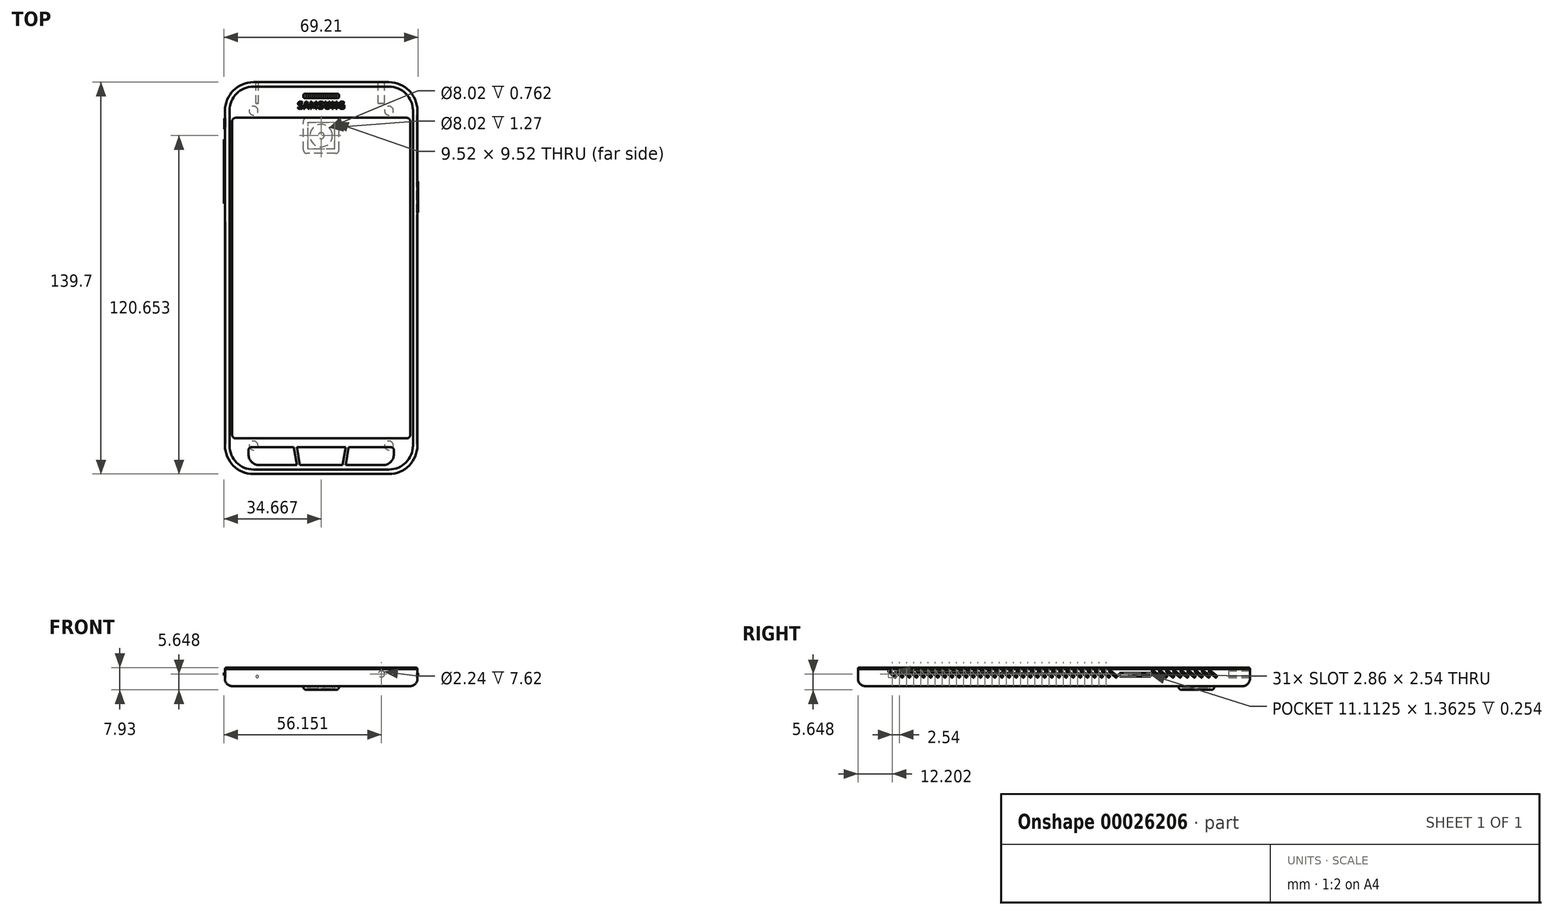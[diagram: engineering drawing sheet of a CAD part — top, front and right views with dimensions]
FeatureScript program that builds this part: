
annotation { "Feature Type Name" : "Feature", "Feature Type Description" : "" }
export const myFeature = defineFeature(function(context is Context, id is Id, definition is map)
    precondition{}
    {
        {
            var Q0;
            Q0=qCreatedBy(makeId("Top.planeOp"),FACE);
            var sketch = newSketch(context, id + "F0", { "sketchPlane" : qUnion([Q0])});
            skLineSegment(sketch, "E0.bottom", {"start": v(-52.33, 67.24) * mm, "end": v(16.25, 67.24) * mm});
            skLineSegment(sketch, "E0.top", {"start": v(-52.33, -72.46) * mm, "end": v(16.25, -72.46) * mm});
            skLineSegment(sketch, "E0.left", {"start": v(-52.33, 67.24) * mm, "end": v(-52.33, -72.46) * mm});
            skLineSegment(sketch, "E0.right", {"start": v(16.25, 67.24) * mm, "end": v(16.25, -72.46) * mm});
            skSolve(sketch);
        }
        {
            var Q0;
            Q0 = qSketchRegion(id + "F0", true);
            extrude(context, id + "F1", {"entities" : qUnion([Q0]), "depth" : 6.1 * mm});
        }
        {
            var Q0;
            Q0=makeQuery(id+"F1.opExtrude","SWEPT_EDGE",EDGE,{"disambiguationData":[OSD([sQuery(id+"F0.wireOp",EDGE,"E0.bottom"),sQuery(id+"F0.wireOp",EDGE,"E0.right")])]});
            var Q1;
            Q1=makeQuery(id+"F1.opExtrude","SWEPT_EDGE",EDGE,{"disambiguationData":[OSD([sQuery(id+"F0.wireOp",EDGE,"E0.top"),sQuery(id+"F0.wireOp",EDGE,"E0.right")])]});
            var Q2;
            Q2=makeQuery(id+"F1.opExtrude","SWEPT_EDGE",EDGE,{"disambiguationData":[OSD([sQuery(id+"F0.wireOp",EDGE,"E0.top"),sQuery(id+"F0.wireOp",EDGE,"E0.left")])]});
            var Q3;
            Q3=makeQuery(id+"F1.opExtrude","SWEPT_EDGE",EDGE,{"disambiguationData":[OSD([sQuery(id+"F0.wireOp",EDGE,"E0.bottom"),sQuery(id+"F0.wireOp",EDGE,"E0.left")])]});
            fillet(context, id + "F2", {"entities" : qUnion([Q0, Q1, Q2, Q3]), "radius" : 10.16 * mm, "tangentPropagation" : true, "allowEdgeOverflow" : false});
        }
        {
            var Q0;
            Q0=makeQuery(id+"F1.opExtrude","CAP_FACE",FACE,{"disambiguationData":[OSD([sQuery(id+"F0.wireOp",EDGE,"E0.bottom"),sQuery(id+"F0.wireOp",EDGE,"E0.top"),sQuery(id+"F0.wireOp",EDGE,"E0.left"),sQuery(id+"F0.wireOp",EDGE,"E0.right")])],"isStart":false});
            var sketch = newSketch(context, id + "F3", { "sketchPlane" : qUnion([Q0])});
            skArc(sketch, "E1.0", {"start": v(13.7, 57.08) * mm, "mid": v(11.48, 62.47) * mm, "end": v(6.09, 64.7) * mm, "construction": true});
            skLineSegment(sketch, "E1.1", {"start": v(13.7, -62.3) * mm, "end": v(13.7, 57.08) * mm, "construction": true});
            skArc(sketch, "E1.2", {"start": v(6.09, -69.92) * mm, "mid": v(11.48, -67.69) * mm, "end": v(13.7, -62.3) * mm, "construction": true});
            skLineSegment(sketch, "E1.3", {"start": v(-42.17, -69.92) * mm, "end": v(6.09, -69.92) * mm, "construction": true});
            skArc(sketch, "E1.4", {"start": v(-49.8, -62.3) * mm, "mid": v(-47.56, -67.69) * mm, "end": v(-42.17, -69.92) * mm, "construction": true});
            skLineSegment(sketch, "E1.5", {"start": v(6.09, 64.7) * mm, "end": v(-42.17, 64.7) * mm, "construction": true});
            skLineSegment(sketch, "E1.6", {"start": v(-49.8, 57.08) * mm, "end": v(-49.8, -62.3) * mm, "construction": true});
            skArc(sketch, "E1.7", {"start": v(-42.17, 64.7) * mm, "mid": v(-47.56, 62.47) * mm, "end": v(-49.8, 57.08) * mm, "construction": true});
            skLineSegment(sketch, "E2.0", {"start": v(-42.17, 54.54) * mm, "end": v(6.09, 54.54) * mm});
            skLineSegment(sketch, "E3.0", {"start": v(-42.17, -59.76) * mm, "end": v(6.09, -59.76) * mm});
            skLineSegment(sketch, "E4", {"start": v(-42.17, 54.54) * mm, "end": v(-48.52, 54.54) * mm});
            skLineSegment(sketch, "E5", {"start": v(6.09, 54.54) * mm, "end": v(12.44, 54.54) * mm});
            skLineSegment(sketch, "E6", {"start": v(6.09, -59.76) * mm, "end": v(12.44, -59.76) * mm});
            skLineSegment(sketch, "E7", {"start": v(13.7, -58.49) * mm, "end": v(13.7, 53.27) * mm});
            skLineSegment(sketch, "E8", {"start": v(-42.17, -59.76) * mm, "end": v(-48.52, -59.76) * mm});
            skLineSegment(sketch, "E9", {"start": v(-49.8, -58.49) * mm, "end": v(-49.8, 53.27) * mm});
            skPoint(sketch, "E10.visualSharp", {"position": v(-49.8, 54.54) * mm});
            skArc(sketch, "E10.filletArc", {"start": v(-48.52, 54.54) * mm, "mid": v(-49.42, 54.17) * mm, "end": v(-49.8, 53.27) * mm});
            skPoint(sketch, "E11.visualSharp", {"position": v(13.7, 54.54) * mm});
            skArc(sketch, "E11.filletArc", {"start": v(13.7, 53.27) * mm, "mid": v(13.34, 54.17) * mm, "end": v(12.44, 54.54) * mm});
            skPoint(sketch, "E12.visualSharp", {"position": v(13.7, -59.76) * mm});
            skArc(sketch, "E12.filletArc", {"start": v(12.44, -59.76) * mm, "mid": v(13.34, -59.39) * mm, "end": v(13.7, -58.49) * mm});
            skPoint(sketch, "E13.visualSharp", {"position": v(-49.8, -59.76) * mm});
            skArc(sketch, "E13.filletArc", {"start": v(-49.8, -58.49) * mm, "mid": v(-49.42, -59.39) * mm, "end": v(-48.52, -59.76) * mm});
            skSolve(sketch);
        }
        {
            var Q0;
            Q0=makeQuery(id+"F3.imprint","IMPRINT",FACE,{"disambiguationData":[TD([[makeQuery(id+"F3.imprint","IMPRINT",EDGE,{"derivedFrom":sQuery(id+"F3.wireOp",EDGE,"E2.0")}),-1.0]])]});
            extrude(context, id + "F4", {"entities" : qUnion([Q0]), "operationType" : NewBodyOperationType.REMOVE, "oppositeDirection" : true, "depth" : 0.03 * mm});
        }
        {
            var Q0;
            Q0 = qSketchRegion(id + "F3", true);
            extrude(context, id + "F5", {"entities" : qUnion([Q0]), "depth" : 0.03 * mm});
        }
        {
            var Q0;
            {var subQ0=sQuery(id+"F0.wireOp",EDGE,"E0.bottom");var subQ1=sQuery(id+"F0.wireOp",EDGE,"E0.right");Q0=makeQuery(id+"F2.opFillet","BLEND_EDGE",EDGE,{"blendedFrom":[makeQuery(id+"F1.opExtrude","SWEPT_EDGE",EDGE,{"disambiguationData":[OSD([subQ0,subQ1])]}),makeQuery(id+"F1.opExtrude","CAP_FACE",FACE,{"disambiguationData":[OSD([subQ0,sQuery(id+"F0.wireOp",EDGE,"E0.top"),sQuery(id+"F0.wireOp",EDGE,"E0.left"),subQ1])],"isStart":true})],"blendedInto":[makeQuery(id+"F1.opExtrude","CAP_FACE",FACE,{"disambiguationData":[OSD([subQ0,sQuery(id+"F0.wireOp",EDGE,"E0.top"),sQuery(id+"F0.wireOp",EDGE,"E0.left"),subQ1])],"isStart":true})]});}
            fillet(context, id + "F6", {"entities" : qUnion([Q0]), "radius" : 2.54 * mm, "tangentPropagation" : true, "allowEdgeOverflow" : false});
        }
        {
            var Q0;
            Q0=makeQuery(id+"F1.opExtrude","CAP_FACE",FACE,{"disambiguationData":[OSD([sQuery(id+"F0.wireOp",EDGE,"E0.bottom"),sQuery(id+"F0.wireOp",EDGE,"E0.top"),sQuery(id+"F0.wireOp",EDGE,"E0.left"),sQuery(id+"F0.wireOp",EDGE,"E0.right")])],"isStart":false});
            var sketch = newSketch(context, id + "F7", { "sketchPlane" : qUnion([Q0])});
            skLineSegment(sketch, "E14", {"start": v(-18.04, 67.24) * mm, "end": v(-18.04, 63.11) * mm, "construction": true});
            skLineSegment(sketch, "E15.0", {"start": v(-48.52, 61.53) * mm, "end": v(12.44, 61.53) * mm, "construction": true});
            skLineSegment(sketch, "E16.bottom", {"start": v(-18.04, 61.53) * mm, "end": v(-11.7, 61.53) * mm});
            skLineSegment(sketch, "E16.top", {"start": v(-18.04, 63.11) * mm, "end": v(-11.7, 63.11) * mm});
            skLineSegment(sketch, "E16.right", {"start": v(-11.7, 61.53) * mm, "end": v(-11.7, 63.11) * mm});
            skLineSegment(sketch, "E17.MirrorCS", {"start": v(-18.04, 63.11) * mm, "end": v(-24.4, 63.11) * mm});
            skLineSegment(sketch, "E18.MirrorCS", {"start": v(-18.04, 61.53) * mm, "end": v(-24.4, 61.53) * mm});
            skLineSegment(sketch, "E19.MirrorCS", {"start": v(-24.4, 61.53) * mm, "end": v(-24.4, 63.11) * mm});
            skLineSegment(sketch, "E20.trimOffspring", {"start": v(-18.04, 61.53) * mm, "end": v(-18.04, -72.46) * mm, "construction": true});
            skArc(sketch, "E21.0", {"start": v(14.66, 57.08) * mm, "mid": v(12.15, 63.14) * mm, "end": v(6.09, 65.65) * mm});
            skLineSegment(sketch, "E21.1", {"start": v(14.66, -62.3) * mm, "end": v(14.66, 57.08) * mm});
            skArc(sketch, "E21.2", {"start": v(6.09, -70.87) * mm, "mid": v(12.15, -68.36) * mm, "end": v(14.66, -62.3) * mm});
            skLineSegment(sketch, "E21.3", {"start": v(-42.17, -70.87) * mm, "end": v(6.09, -70.87) * mm});
            skArc(sketch, "E21.4", {"start": v(-50.75, -62.3) * mm, "mid": v(-48.23, -68.36) * mm, "end": v(-42.17, -70.87) * mm});
            skLineSegment(sketch, "E21.5", {"start": v(6.09, 65.65) * mm, "end": v(-42.17, 65.65) * mm});
            skLineSegment(sketch, "E21.6", {"start": v(-50.75, 57.08) * mm, "end": v(-50.75, -62.3) * mm});
            skArc(sketch, "E21.7", {"start": v(-42.17, 65.65) * mm, "mid": v(-48.23, 63.14) * mm, "end": v(-50.75, 57.08) * mm});
            skArc(sketch, "E22.0", {"start": v(16.25, 57.08) * mm, "mid": v(13.27, 64.27) * mm, "end": v(6.09, 67.24) * mm});
            skLineSegment(sketch, "E22.1", {"start": v(16.25, -62.3) * mm, "end": v(16.25, 57.08) * mm});
            skArc(sketch, "E22.2", {"start": v(6.09, -72.46) * mm, "mid": v(13.27, -69.48) * mm, "end": v(16.25, -62.3) * mm});
            skLineSegment(sketch, "E22.3", {"start": v(-42.17, -72.46) * mm, "end": v(6.09, -72.46) * mm});
            skArc(sketch, "E22.4", {"start": v(-52.33, -62.3) * mm, "mid": v(-49.36, -69.48) * mm, "end": v(-42.17, -72.46) * mm});
            skLineSegment(sketch, "E22.5", {"start": v(6.09, 67.24) * mm, "end": v(-42.17, 67.24) * mm});
            skLineSegment(sketch, "E22.6", {"start": v(-52.33, 57.08) * mm, "end": v(-52.33, -62.3) * mm});
            skArc(sketch, "E22.7", {"start": v(-42.17, 67.24) * mm, "mid": v(-49.36, 64.27) * mm, "end": v(-52.33, 57.08) * mm});
            skLineSegment(sketch, "E23.0", {"start": v(12.44, -69.28) * mm, "end": v(-47.5, -69.28) * mm, "construction": true});
            skLineSegment(sketch, "E24.bottom", {"start": v(-17.53, -69.28) * mm, "end": v(-7.82, -69.28) * mm});
            skLineSegment(sketch, "E24.top", {"start": v(-18.55, -62.93) * mm, "end": v(-9.34, -62.93) * mm});
            skLineSegment(sketch, "E24.right", {"start": v(7.87, -65.47) * mm, "end": v(7.87, -63.95) * mm});
            skLineSegment(sketch, "E25.MirrorCS", {"start": v(-17.53, -62.93) * mm, "end": v(-26.75, -62.93) * mm});
            skLineSegment(sketch, "E26.MirrorCS", {"start": v(-43.95, -65.47) * mm, "end": v(-43.95, -63.95) * mm});
            skLineSegment(sketch, "E27.MirrorCS", {"start": v(-18.55, -69.28) * mm, "end": v(-28.27, -69.28) * mm});
            skPoint(sketch, "E28.visualSharp", {"position": v(-43.95, -62.93) * mm});
            skArc(sketch, "E28.filletArc", {"start": v(-42.93, -62.93) * mm, "mid": v(-43.65, -63.23) * mm, "end": v(-43.95, -63.95) * mm});
            skPoint(sketch, "E29.visualSharp", {"position": v(7.87, -62.93) * mm});
            skArc(sketch, "E29.filletArc", {"start": v(7.87, -63.95) * mm, "mid": v(7.57, -63.23) * mm, "end": v(6.85, -62.93) * mm});
            skPoint(sketch, "E30.visualSharp", {"position": v(-43.95, -69.28) * mm});
            skArc(sketch, "E30.filletArc", {"start": v(-43.95, -65.47) * mm, "mid": v(-42.83, -68.17) * mm, "end": v(-40.14, -69.28) * mm});
            skPoint(sketch, "E31.visualSharp", {"position": v(7.87, -69.28) * mm});
            skArc(sketch, "E31.filletArc", {"start": v(4.06, -69.28) * mm, "mid": v(6.75, -68.17) * mm, "end": v(7.87, -65.47) * mm});
            skLineSegment(sketch, "E32", {"start": v(-18.04, -66.4) * mm, "end": v(-8.52, -66.4) * mm, "construction": true});
            skLineSegment(sketch, "E33.trimOffspring", {"start": v(-27.84, -62.93) * mm, "end": v(-42.93, -62.93) * mm});
            skLineSegment(sketch, "E34.trimOffspring", {"start": v(-29.36, -69.28) * mm, "end": v(-40.14, -69.28) * mm});
            skLineSegment(sketch, "E35.trimOffspring", {"start": v(-8.25, -62.93) * mm, "end": v(6.85, -62.93) * mm});
            skLineSegment(sketch, "E36.trimOffspring", {"start": v(-6.73, -69.28) * mm, "end": v(4.06, -69.28) * mm});
            skLineSegment(sketch, "E37", {"start": v(-18.55, -69.28) * mm, "end": v(-17.53, -69.28) * mm});
            skLineSegment(sketch, "E38", {"start": v(-24.4, 62.32) * mm, "end": v(-11.7, 62.32) * mm, "construction": true});
            skCircle(sketch, "E39", {"center": v(-18.04, 62.32) * mm, "radius": 0.13 * mm});
            skCircle(sketch, "E40.1.0.0", {"center": v(-17.28, 62.32) * mm, "radius": 0.13 * mm});
            skCircle(sketch, "E40.2.0.0", {"center": v(-16.52, 62.32) * mm, "radius": 0.13 * mm});
            skCircle(sketch, "E40.3.0.0", {"center": v(-15.76, 62.32) * mm, "radius": 0.13 * mm});
            skCircle(sketch, "E40.4.0.0", {"center": v(-15, 62.32) * mm, "radius": 0.13 * mm});
            skCircle(sketch, "E40.5.0.0", {"center": v(-14.23, 62.32) * mm, "radius": 0.13 * mm});
            skCircle(sketch, "E40.6.0.0", {"center": v(-13.47, 62.32) * mm, "radius": 0.13 * mm});
            skCircle(sketch, "E40.7.0.0", {"center": v(-12.7, 62.32) * mm, "radius": 0.13 * mm});
            skLineSegment(sketch, "E40.direction1", {"start": v(-18.04, 62.32) * mm, "end": v(-17.28, 62.32) * mm, "construction": true});
            skCircle(sketch, "E41.1.0.0", {"center": v(-18.8, 62.32) * mm, "radius": 0.13 * mm});
            skCircle(sketch, "E41.2.0.0", {"center": v(-19.57, 62.32) * mm, "radius": 0.13 * mm});
            skCircle(sketch, "E41.3.0.0", {"center": v(-20.33, 62.32) * mm, "radius": 0.13 * mm});
            skCircle(sketch, "E41.4.0.0", {"center": v(-21.1, 62.32) * mm, "radius": 0.13 * mm});
            skCircle(sketch, "E41.5.0.0", {"center": v(-21.85, 62.32) * mm, "radius": 0.13 * mm});
            skCircle(sketch, "E41.6.0.0", {"center": v(-22.61, 62.32) * mm, "radius": 0.13 * mm});
            skCircle(sketch, "E41.7.0.0", {"center": v(-23.38, 62.32) * mm, "radius": 0.13 * mm});
            skLineSegment(sketch, "E41.direction1", {"start": v(-18.04, 62.32) * mm, "end": v(-18.8, 62.32) * mm, "construction": true});
            skLineSegment(sketch, "E42", {"start": v(-26.75, -62.93) * mm, "end": v(-27.84, -62.93) * mm});
            skLineSegment(sketch, "E43", {"start": v(-28.27, -69.28) * mm, "end": v(-29.36, -69.28) * mm});
            skLineSegment(sketch, "E44", {"start": v(-9.34, -62.93) * mm, "end": v(-8.25, -62.93) * mm});
            skLineSegment(sketch, "E45", {"start": v(-6.73, -69.28) * mm, "end": v(-7.82, -69.28) * mm});
            skLineSegment(sketch, "E46", {"start": v(-8.25, -62.93) * mm, "end": v(-9.34, -69.28) * mm});
            skLineSegment(sketch, "E47", {"start": v(-10.43, -62.93) * mm, "end": v(-10.43, -69.28) * mm, "construction": true});
            skPoint(sketch, "E48.MirrorCS.end.orphan", {"position": v(-10.86, -69.28) * mm});
            skLineSegment(sketch, "E49", {"start": v(-9.34, -62.93) * mm, "end": v(-10.43, -69.28) * mm});
            skPoint(sketch, "E50.orphan", {"position": v(-7.82, -69.28) * mm});
            skPoint(sketch, "E51.MirrorCS.start.orphan", {"position": v(-9.34, -62.93) * mm});
            skLineSegment(sketch, "E52.MirrorCS", {"start": v(-26.75, -62.93) * mm, "end": v(-25.65, -69.28) * mm});
            skLineSegment(sketch, "E53.MirrorCS", {"start": v(-27.84, -62.93) * mm, "end": v(-26.75, -69.28) * mm});
            skSolve(sketch);
        }
        {
            var Q0;
            Q0=makeQuery(id+"F7.imprint","IMPRINT",FACE,{"disambiguationData":[TD([[makeQuery(id+"F7.imprint","IMPRINT",EDGE,{"derivedFrom":sQuery(id+"F7.wireOp",EDGE,"E16.bottom")}),1.0]])]});
            var Q1;
            Q1=makeQuery(id+"F7.imprint","IMPRINT",FACE,{"disambiguationData":[TD([[makeQuery(id+"F7.imprint","IMPRINT",EDGE,{"derivedFrom":sQuery(id+"F7.wireOp",EDGE,"E21.0")}),-1.0]])]});
            var Q2;
            Q2=makeQuery(id+"F7.imprint","IMPRINT",FACE,{"disambiguationData":[TD([[makeQuery(id+"F7.imprint","IMPRINT",EDGE,{"derivedFrom":sQuery(id+"F7.wireOp",EDGE,"E26.MirrorCS")}),-1.0]])]});
            var Q3;
            Q3=makeQuery(id+"F7.imprint","IMPRINT",FACE,{"disambiguationData":[TD([[makeQuery(id+"F7.imprint","IMPRINT",EDGE,{"derivedFrom":sQuery(id+"F7.wireOp",EDGE,"E24.right")}),1.0]])]});
            var Q4;
            {var subQ6=sQuery(id+"F7.wireOp",EDGE,"E24.top");Q4=makeQuery(id+"F7.imprint","IMPRINT",FACE,{"disambiguationData":[TD([[makeQuery(id+"F7.imprint","IMPRINT",EDGE,{"derivedFrom":subQ6}),-1.0]])]});}
            extrude(context, id + "F8", {"entities" : qUnion([Q0, Q1, Q2, Q3, Q4]), "depth" : 0.5 * mm});
        }
        {
            var Q0;
            Q0=makeQuery(id+"F8.opExtrude","SWEPT_EDGE",EDGE,{"disambiguationData":[OSD([sQuery(id+"F7.wireOp",EDGE,"E16.top"),sQuery(id+"F7.wireOp",EDGE,"E16.right")])]});
            var Q1;
            Q1=makeQuery(id+"F8.opExtrude","SWEPT_EDGE",EDGE,{"disambiguationData":[OSD([sQuery(id+"F7.wireOp",EDGE,"E16.bottom"),sQuery(id+"F7.wireOp",EDGE,"E16.right")])]});
            var Q2;
            Q2=makeQuery(id+"F8.opExtrude","SWEPT_EDGE",EDGE,{"disambiguationData":[OSD([sQuery(id+"F7.wireOp",EDGE,"E19.MirrorCS"),sQuery(id+"F7.wireOp",EDGE,"E18.MirrorCS")])]});
            var Q3;
            Q3=makeQuery(id+"F8.opExtrude","SWEPT_EDGE",EDGE,{"disambiguationData":[OSD([sQuery(id+"F7.wireOp",EDGE,"E17.MirrorCS"),sQuery(id+"F7.wireOp",EDGE,"E19.MirrorCS")])]});
            fillet(context, id + "F9", {"entities" : qUnion([Q0, Q1, Q2, Q3]), "radius" : 0.5 * mm, "tangentPropagation" : true, "allowEdgeOverflow" : false});
        }
        {
            var Q0;
            Q0=makeQuery(id+"F8.opExtrude","CAP_EDGE",EDGE,{"disambiguationData":[OSD([sQuery(id+"F7.wireOp",EDGE,"E21.6")])],"isStart":false});
            var Q1;
            Q1=makeQuery(id+"F8.opExtrude","CAP_EDGE",EDGE,{"disambiguationData":[OSD([sQuery(id+"F7.wireOp",EDGE,"E21.1")])],"isStart":false});
            var Q2;
            Q2=makeQuery(id+"F8.opExtrude","CAP_EDGE",EDGE,{"disambiguationData":[OSD([sQuery(id+"F7.wireOp",EDGE,"E21.5")])],"isStart":false});
            var Q3;
            Q3=makeQuery(id+"F8.opExtrude","CAP_EDGE",EDGE,{"disambiguationData":[OSD([sQuery(id+"F7.wireOp",EDGE,"E21.0")])],"isStart":false});
            var Q4;
            Q4=makeQuery(id+"F8.opExtrude","CAP_EDGE",EDGE,{"disambiguationData":[OSD([sQuery(id+"F7.wireOp",EDGE,"E21.7")])],"isStart":false});
            var Q5;
            Q5=makeQuery(id+"F8.opExtrude","CAP_EDGE",EDGE,{"disambiguationData":[OSD([sQuery(id+"F7.wireOp",EDGE,"E21.2")])],"isStart":false});
            var Q6;
            Q6=makeQuery(id+"F8.opExtrude","CAP_EDGE",EDGE,{"disambiguationData":[OSD([sQuery(id+"F7.wireOp",EDGE,"E21.3")])],"isStart":false});
            var Q7;
            Q7=makeQuery(id+"F8.opExtrude","CAP_EDGE",EDGE,{"disambiguationData":[OSD([sQuery(id+"F7.wireOp",EDGE,"E21.4")])],"isStart":false});
            fillet(context, id + "F10", {"entities" : qUnion([Q0, Q1, Q2, Q3, Q4, Q5, Q6, Q7]), "radius" : 0.5 * mm, "tangentPropagation" : true, "allowEdgeOverflow" : false});
        }
        {
            var Q0;
            Q0=makeQuery(id+"F8.opExtrude","CAP_EDGE",EDGE,{"disambiguationData":[OSD([sQuery(id+"F7.wireOp",EDGE,"E22.1")])],"isStart":false});
            var Q1;
            Q1=makeQuery(id+"F8.opExtrude","CAP_EDGE",EDGE,{"disambiguationData":[OSD([sQuery(id+"F7.wireOp",EDGE,"E22.0")])],"isStart":false});
            var Q2;
            Q2=makeQuery(id+"F8.opExtrude","CAP_EDGE",EDGE,{"disambiguationData":[OSD([sQuery(id+"F7.wireOp",EDGE,"E22.5")])],"isStart":false});
            var Q3;
            Q3=makeQuery(id+"F8.opExtrude","CAP_EDGE",EDGE,{"disambiguationData":[OSD([sQuery(id+"F7.wireOp",EDGE,"E22.7")])],"isStart":false});
            var Q4;
            Q4=makeQuery(id+"F8.opExtrude","CAP_EDGE",EDGE,{"disambiguationData":[OSD([sQuery(id+"F7.wireOp",EDGE,"E22.6")])],"isStart":false});
            var Q5;
            Q5=makeQuery(id+"F8.opExtrude","CAP_EDGE",EDGE,{"disambiguationData":[OSD([sQuery(id+"F7.wireOp",EDGE,"E22.4")])],"isStart":false});
            var Q6;
            Q6=makeQuery(id+"F8.opExtrude","CAP_EDGE",EDGE,{"disambiguationData":[OSD([sQuery(id+"F7.wireOp",EDGE,"E22.3")])],"isStart":false});
            var Q7;
            Q7=makeQuery(id+"F8.opExtrude","CAP_EDGE",EDGE,{"disambiguationData":[OSD([sQuery(id+"F7.wireOp",EDGE,"E22.2")])],"isStart":false});
            fillet(context, id + "F11", {"entities" : qUnion([Q0, Q1, Q2, Q3, Q4, Q5, Q6, Q7]), "radius" : 0.5 * mm, "tangentPropagation" : true, "allowEdgeOverflow" : false});
        }
        {
            var Q0;
            Q0=makeQuery(id+"F1.opExtrude","CAP_FACE",FACE,{"disambiguationData":[OSD([sQuery(id+"F0.wireOp",EDGE,"E0.bottom"),sQuery(id+"F0.wireOp",EDGE,"E0.top"),sQuery(id+"F0.wireOp",EDGE,"E0.left"),sQuery(id+"F0.wireOp",EDGE,"E0.right")])],"isStart":true});
            var sketch = newSketch(context, id + "F12", { "sketchPlane" : qUnion([Q0])});
            skPoint(sketch, "E54.visualSharp", {"position": v(-24.4, 59.76) * mm});
            skPoint(sketch, "E55.visualSharp", {"position": v(-11.7, 59.76) * mm});
            skPoint(sketch, "E56.visualSharp", {"position": v(-11.7, 47.06) * mm});
            skPoint(sketch, "E57.visualSharp", {"position": v(-24.4, 47.06) * mm});
            skLineSegment(sketch, "E58", {"start": v(-49.8, 2.6) * mm, "end": v(13.7, 2.6) * mm, "construction": true});
            skLineSegment(sketch, "E59.MirrorCS", {"start": v(-18.04, -52.95) * mm, "end": v(-22.8, -52.95) * mm});
            skLineSegment(sketch, "E60.MirrorCS", {"start": v(-13.28, -43.43) * mm, "end": v(-13.28, -52.95) * mm});
            skLineSegment(sketch, "E61.MirrorCS", {"start": v(-22.8, -43.43) * mm, "end": v(-22.8, -52.95) * mm});
            skLineSegment(sketch, "E62.MirrorCS", {"start": v(-18.04, -52.95) * mm, "end": v(-13.28, -52.95) * mm});
            skLineSegment(sketch, "E63.MirrorCS", {"start": v(-18.04, -43.43) * mm, "end": v(-13.28, -43.43) * mm});
            skLineSegment(sketch, "E64.MirrorCS", {"start": v(-42.17, -41.84) * mm, "end": v(6.09, -41.84) * mm, "construction": true});
            skArc(sketch, "E65.MirrorCS", {"start": v(-12.96, -41.84) * mm, "mid": v(-12.06, -42.21) * mm, "end": v(-11.7, -43.11) * mm});
            skLineSegment(sketch, "E66.MirrorCS", {"start": v(-24.4, -43.11) * mm, "end": v(-24.4, -53.27) * mm});
            skLineSegment(sketch, "E67.MirrorCS", {"start": v(-11.7, -43.11) * mm, "end": v(-11.7, -53.27) * mm});
            skArc(sketch, "E68.MirrorCS", {"start": v(-11.7, -53.27) * mm, "mid": v(-12.06, -54.17) * mm, "end": v(-12.96, -54.54) * mm});
            skLineSegment(sketch, "E69.MirrorCS", {"start": v(-18.04, -54.54) * mm, "end": v(-12.96, -54.54) * mm});
            skArc(sketch, "E70.MirrorCS", {"start": v(-23.12, -54.54) * mm, "mid": v(-24.02, -54.17) * mm, "end": v(-24.4, -53.27) * mm});
            skLineSegment(sketch, "E71.MirrorCS", {"start": v(-18.04, -54.54) * mm, "end": v(-23.12, -54.54) * mm});
            skPoint(sketch, "E72.orphan", {"position": v(6.09, 47.06) * mm});
            skPoint(sketch, "E73.orphan", {"position": v(-42.17, 47.06) * mm});
            skLineSegment(sketch, "E74.MirrorCS", {"start": v(-18.04, -41.84) * mm, "end": v(-12.96, -41.84) * mm, "construction": true});
            skLineSegment(sketch, "E75.MirrorCS", {"start": v(-18.04, -41.84) * mm, "end": v(-23.12, -41.84) * mm});
            skLineSegment(sketch, "E76", {"start": v(-12.96, -41.84) * mm, "end": v(-18.04, -41.84) * mm});
            skPoint(sketch, "E77.top.start.orphan", {"position": v(-18.04, 59.76) * mm});
            skPoint(sketch, "E78.orphan", {"position": v(-18.04, 69.92) * mm});
            skPoint(sketch, "E54.filletArc.start.orphan", {"position": v(-23.12, 59.76) * mm});
            skPoint(sketch, "E79.MirrorCS.end.orphan", {"position": v(-24.4, 58.49) * mm});
            skPoint(sketch, "E80.MirrorCS.end.orphan", {"position": v(-22.8, 58.17) * mm});
            skPoint(sketch, "E80.MirrorCS.start.orphan", {"position": v(-22.8, 48.65) * mm});
            skPoint(sketch, "E81.5.end.orphan", {"position": v(-13.28, 58.17) * mm});
            skPoint(sketch, "E55.filletArc.end.orphan", {"position": v(-12.96, 59.76) * mm});
            skPoint(sketch, "E55.filletArc.start.orphan", {"position": v(-11.7, 58.49) * mm});
            skPoint(sketch, "E81.1.start.orphan", {"position": v(-18.04, 58.17) * mm});
            skPoint(sketch, "E81.4.end.orphan", {"position": v(-13.28, 48.65) * mm});
            skPoint(sketch, "E81.4.start.orphan", {"position": v(-18.04, 48.65) * mm});
            skPoint(sketch, "E82.MirrorCS.end.orphan", {"position": v(-23.12, -41.84) * mm});
            skPoint(sketch, "E82.MirrorCS.start.orphan", {"position": v(-24.4, -43.11) * mm});
            skPoint(sketch, "E56.filletArc.end.orphan", {"position": v(-11.7, 48.33) * mm});
            skPoint(sketch, "E83.MirrorCS.end.orphan", {"position": v(-22.8, -43.43) * mm});
            skPoint(sketch, "E83.MirrorCS.start.orphan", {"position": v(-18.04, -43.43) * mm});
            skPoint(sketch, "E77.bottom.end.orphan", {"position": v(-12.96, 47.06) * mm});
            skPoint(sketch, "E77.bottom.start.orphan", {"position": v(-18.04, 47.06) * mm});
            skPoint(sketch, "E57.filletArc.end.orphan", {"position": v(-23.12, 47.06) * mm});
            skPoint(sketch, "E57.filletArc.start.orphan", {"position": v(-24.4, 48.33) * mm});
            skLineSegment(sketch, "E84", {"start": v(-18.04, -43.43) * mm, "end": v(-22.8, -43.43) * mm});
            skArc(sketch, "E85", {"start": v(-23.12, -41.84) * mm, "mid": v(-24.02, -42.21) * mm, "end": v(-24.4, -43.11) * mm});
            skLineSegment(sketch, "E86", {"start": v(-42.17, -64.7) * mm, "end": v(-42.17, 69.92) * mm, "construction": true});
            skLineSegment(sketch, "E87", {"start": v(6.09, 69.92) * mm, "end": v(6.09, -64.7) * mm, "construction": true});
            skLineSegment(sketch, "E88", {"start": v(13.7, -57.08) * mm, "end": v(-49.8, -57.08) * mm, "construction": true});
            skLineSegment(sketch, "E89", {"start": v(13.7, 62.3) * mm, "end": v(-49.8, 62.3) * mm, "construction": true});
            skCircle(sketch, "E90", {"center": v(-42.17, 62.3) * mm, "radius": 1.59 * mm});
            skCircle(sketch, "E91", {"center": v(6.09, 62.3) * mm, "radius": 1.59 * mm});
            skCircle(sketch, "E92", {"center": v(-42.17, -57.08) * mm, "radius": 1.59 * mm});
            skCircle(sketch, "E93", {"center": v(6.09, -57.08) * mm, "radius": 1.59 * mm});
            skSolve(sketch);
        }
        {
            var Q0;
            Q0=makeQuery(id+"F12.imprint","IMPRINT",FACE,{"disambiguationData":[TD([[makeQuery(id+"F12.imprint","IMPRINT",EDGE,{"derivedFrom":sQuery(id+"F12.wireOp",EDGE,"E59.MirrorCS")}),1.0]])]});
            extrude(context, id + "F13", {"entities" : qUnion([Q0]), "operationType" : NewBodyOperationType.ADD, "depth" : 1.33 * mm});
        }
        {
            var Q0;
            Q0=makeQuery(id+"F13.boolean.opBoolean","SPLIT",FACE,{"disambiguationData":[TD([makeQuery(id+"F13.opExtrude","SWEPT_FACE",FACE,{"disambiguationData":[OSD([sQuery(id+"F12.wireOp",EDGE,"E60.MirrorCS")])]})])],"derivedFrom":makeQuery(id+"F1.opExtrude","CAP_FACE",FACE,{"disambiguationData":[OSD([sQuery(id+"F0.wireOp",EDGE,"E0.bottom"),sQuery(id+"F0.wireOp",EDGE,"E0.top"),sQuery(id+"F0.wireOp",EDGE,"E0.left"),sQuery(id+"F0.wireOp",EDGE,"E0.right")])],"isStart":true})});
            var sketch = newSketch(context, id + "F14", { "sketchPlane" : qUnion([Q0])});
            skLineSegment(sketch, "E94.bottom", {"start": v(-22.8, -43.43) * mm, "end": v(-13.28, -43.43) * mm});
            skLineSegment(sketch, "E94.top", {"start": v(-22.8, -52.95) * mm, "end": v(-13.28, -52.95) * mm});
            skLineSegment(sketch, "E94.left", {"start": v(-22.8, -43.43) * mm, "end": v(-22.8, -52.95) * mm});
            skLineSegment(sketch, "E94.right", {"start": v(-13.28, -43.43) * mm, "end": v(-13.28, -52.95) * mm});
            skLineSegment(sketch, "E95", {"start": v(-18.04, -52.95) * mm, "end": v(-18.04, -43.43) * mm, "construction": true});
            skLineSegment(sketch, "E96", {"start": v(-13.28, -48.2) * mm, "end": v(-22.8, -48.2) * mm, "construction": true});
            skCircle(sketch, "E97", {"center": v(-18.04, -48.2) * mm, "radius": 4 * mm});
            skCircle(sketch, "E98", {"center": v(-18.04, -48.2) * mm, "radius": 1.08 * mm});
            skSolve(sketch);
        }
        {
            var Q0;
            Q0 = qSketchRegion(id + "F14", true);
            var Q1;
            Q1=makeQuery(id+"F14.imprint","IMPRINT",FACE,{"disambiguationData":[TD([[makeQuery(id+"F14.imprint","IMPRINT",EDGE,{"derivedFrom":sQuery(id+"F14.wireOp",EDGE,"E98")}),1.0]])]});
            extrude(context, id + "F15", {"entities" : qUnion([Q0, Q1]), "depth" : 1.27 * mm});
        }
        {
            var Q0;
            Q0=makeQuery(id+"F13.opExtrude","CAP_EDGE",EDGE,{"disambiguationData":[OSD([sQuery(id+"F12.wireOp",EDGE,"E67.MirrorCS")])],"isStart":false});
            var Q1;
            Q1=makeQuery(id+"F13.opExtrude","CAP_EDGE",EDGE,{"disambiguationData":[OSD([sQuery(id+"F12.wireOp",EDGE,"E68.MirrorCS")])],"isStart":false});
            var Q2;
            Q2=makeQuery(id+"F13.opExtrude","CAP_EDGE",EDGE,{"disambiguationData":[OSD([sQuery(id+"F12.wireOp",EDGE,"E65.MirrorCS")])],"isStart":false});
            var Q3;
            Q3=makeQuery(id+"F13.opExtrude","CAP_EDGE",EDGE,{"disambiguationData":[OSD([sQuery(id+"F12.wireOp",EDGE,"E75.MirrorCS"),sQuery(id+"F12.wireOp",EDGE,"E76")])],"isStart":false});
            var Q4;
            Q4=makeQuery(id+"F13.opExtrude","CAP_EDGE",EDGE,{"disambiguationData":[OSD([sQuery(id+"F12.wireOp",EDGE,"E85")])],"isStart":false});
            var Q5;
            Q5=makeQuery(id+"F13.opExtrude","CAP_EDGE",EDGE,{"disambiguationData":[OSD([sQuery(id+"F12.wireOp",EDGE,"E66.MirrorCS")])],"isStart":false});
            var Q6;
            Q6=makeQuery(id+"F13.opExtrude","CAP_EDGE",EDGE,{"disambiguationData":[OSD([sQuery(id+"F12.wireOp",EDGE,"E70.MirrorCS")])],"isStart":false});
            var Q7;
            Q7=makeQuery(id+"F13.opExtrude","CAP_EDGE",EDGE,{"disambiguationData":[OSD([sQuery(id+"F12.wireOp",EDGE,"E69.MirrorCS"),sQuery(id+"F12.wireOp",EDGE,"E71.MirrorCS")])],"isStart":false});
            fillet(context, id + "F16", {"entities" : qUnion([Q0, Q1, Q2, Q3, Q4, Q5, Q6, Q7]), "radius" : 1.02 * mm, "tangentPropagation" : true, "allowEdgeOverflow" : false});
        }
        {
            var Q0;
            Q0=makeQuery(id+"F1.opExtrude","SWEPT_FACE",FACE,{"disambiguationData":[OSD([sQuery(id+"F0.wireOp",EDGE,"E0.left")])]});
            var sketch = newSketch(context, id + "F17", { "sketchPlane" : qUnion([Q0])});
            skLineSegment(sketch, "E99", {"start": v(61.3, 6.1) * mm, "end": v(61.3, 5.2) * mm, "construction": true});
            skPoint(sketch, "E100.end.orphan", {"position": v(61.3, 5.2) * mm});
            skPoint(sketch, "E101.start.orphan", {"position": v(59.2, 3.43) * mm});
            skPoint(sketch, "E102.start.orphan", {"position": v(59.2, 2.54) * mm});
            skLineSegment(sketch, "E103", {"start": v(59.2, 2.54) * mm, "end": v(59.2, 6.1) * mm, "construction": true});
            skLineSegment(sketch, "E104", {"start": v(61.3, 6.1) * mm, "end": v(61.3, 2.54) * mm, "construction": true});
            skLineSegment(sketch, "E105", {"start": v(61.3, 4.32) * mm, "end": v(59.2, 4.32) * mm, "construction": true});
            skLineSegment(sketch, "E106", {"start": v(59.2, 4.32) * mm, "end": v(59.2, 3.43) * mm, "construction": true});
            skLineSegment(sketch, "E107", {"start": v(61.3, 4.32) * mm, "end": v(61.3, 5.2) * mm, "construction": true});
            skLineSegment(sketch, "E108", {"start": v(58.72, 4.01) * mm, "end": v(60.81, 5.79) * mm, "construction": true});
            skLineSegment(sketch, "E109", {"start": v(61.06, 5.5) * mm, "end": v(60.81, 5.79) * mm, "construction": true});
            skLineSegment(sketch, "E110", {"start": v(58.96, 3.72) * mm, "end": v(58.72, 4.01) * mm, "construction": true});
            skLineSegment(sketch, "E111", {"start": v(59.2, 3.43) * mm, "end": v(61.3, 5.2) * mm, "construction": true});
            skLineSegment(sketch, "E112", {"start": v(59.46, 3.14) * mm, "end": v(61.55, 4.92) * mm});
            skLineSegment(sketch, "E113", {"start": v(61.06, 5.5) * mm, "end": v(58.96, 3.72) * mm});
            skArc(sketch, "E114", {"start": v(58.96, 3.72) * mm, "mid": v(58.92, 3.18) * mm, "end": v(59.46, 3.14) * mm});
            skArc(sketch, "E115", {"start": v(61.55, 4.92) * mm, "mid": v(61.6, 5.45) * mm, "end": v(61.06, 5.5) * mm});
            skLineSegment(sketch, "E116", {"start": v(61.3, 3.55) * mm, "end": v(62.3, 3.55) * mm, "construction": true});
            skLineSegment(sketch, "E117.1.0.0", {"start": v(58.52, 5.5) * mm, "end": v(56.42, 3.72) * mm});
            skArc(sketch, "E117.1.0.1", {"start": v(59.01, 4.92) * mm, "mid": v(59.06, 5.45) * mm, "end": v(58.52, 5.5) * mm});
            skLineSegment(sketch, "E117.1.0.2", {"start": v(56.92, 3.14) * mm, "end": v(59.01, 4.92) * mm});
            skArc(sketch, "E117.1.0.3", {"start": v(56.42, 3.72) * mm, "mid": v(56.38, 3.18) * mm, "end": v(56.92, 3.14) * mm});
            skLineSegment(sketch, "E117.2.0.0", {"start": v(55.98, 5.5) * mm, "end": v(53.88, 3.72) * mm});
            skArc(sketch, "E117.2.0.1", {"start": v(56.47, 4.92) * mm, "mid": v(56.52, 5.45) * mm, "end": v(55.98, 5.5) * mm});
            skLineSegment(sketch, "E117.2.0.2", {"start": v(54.38, 3.14) * mm, "end": v(56.47, 4.92) * mm});
            skArc(sketch, "E117.2.0.3", {"start": v(53.88, 3.72) * mm, "mid": v(53.84, 3.18) * mm, "end": v(54.38, 3.14) * mm});
            skLineSegment(sketch, "E117.3.0.0", {"start": v(53.44, 5.5) * mm, "end": v(51.34, 3.72) * mm});
            skArc(sketch, "E117.3.0.1", {"start": v(53.93, 4.92) * mm, "mid": v(53.98, 5.45) * mm, "end": v(53.44, 5.5) * mm});
            skLineSegment(sketch, "E117.3.0.2", {"start": v(51.84, 3.14) * mm, "end": v(53.93, 4.92) * mm});
            skArc(sketch, "E117.3.0.3", {"start": v(51.34, 3.72) * mm, "mid": v(51.3, 3.18) * mm, "end": v(51.84, 3.14) * mm});
            skLineSegment(sketch, "E117.4.0.0", {"start": v(50.9, 5.5) * mm, "end": v(48.8, 3.72) * mm});
            skArc(sketch, "E117.4.0.1", {"start": v(51.4, 4.92) * mm, "mid": v(51.44, 5.45) * mm, "end": v(50.9, 5.5) * mm});
            skLineSegment(sketch, "E117.4.0.2", {"start": v(49.3, 3.14) * mm, "end": v(51.4, 4.92) * mm});
            skArc(sketch, "E117.4.0.3", {"start": v(48.8, 3.72) * mm, "mid": v(48.76, 3.18) * mm, "end": v(49.3, 3.14) * mm});
            skLineSegment(sketch, "E117.5.0.0", {"start": v(48.36, 5.5) * mm, "end": v(46.26, 3.72) * mm});
            skArc(sketch, "E117.5.0.1", {"start": v(48.85, 4.92) * mm, "mid": v(48.9, 5.45) * mm, "end": v(48.36, 5.5) * mm});
            skLineSegment(sketch, "E117.5.0.2", {"start": v(46.76, 3.14) * mm, "end": v(48.85, 4.92) * mm});
            skArc(sketch, "E117.5.0.3", {"start": v(46.26, 3.72) * mm, "mid": v(46.22, 3.18) * mm, "end": v(46.76, 3.14) * mm});
            skLineSegment(sketch, "E117.6.0.0", {"start": v(45.82, 5.5) * mm, "end": v(43.72, 3.72) * mm});
            skArc(sketch, "E117.6.0.1", {"start": v(46.31, 4.92) * mm, "mid": v(46.36, 5.45) * mm, "end": v(45.82, 5.5) * mm});
            skLineSegment(sketch, "E117.6.0.2", {"start": v(44.22, 3.14) * mm, "end": v(46.31, 4.92) * mm});
            skArc(sketch, "E117.6.0.3", {"start": v(43.72, 3.72) * mm, "mid": v(43.68, 3.18) * mm, "end": v(44.22, 3.14) * mm});
            skLineSegment(sketch, "E117.7.0.0", {"start": v(43.28, 5.5) * mm, "end": v(41.18, 3.72) * mm});
            skArc(sketch, "E117.7.0.1", {"start": v(43.77, 4.92) * mm, "mid": v(43.82, 5.45) * mm, "end": v(43.28, 5.5) * mm});
            skLineSegment(sketch, "E117.7.0.2", {"start": v(41.68, 3.14) * mm, "end": v(43.77, 4.92) * mm});
            skArc(sketch, "E117.7.0.3", {"start": v(41.18, 3.72) * mm, "mid": v(41.14, 3.18) * mm, "end": v(41.68, 3.14) * mm});
            skLineSegment(sketch, "E117.8.0.0", {"start": v(40.74, 5.5) * mm, "end": v(38.64, 3.72) * mm});
            skArc(sketch, "E117.8.0.1", {"start": v(41.23, 4.92) * mm, "mid": v(41.28, 5.45) * mm, "end": v(40.74, 5.5) * mm});
            skLineSegment(sketch, "E117.8.0.2", {"start": v(39.14, 3.14) * mm, "end": v(41.23, 4.92) * mm});
            skArc(sketch, "E117.8.0.3", {"start": v(38.64, 3.72) * mm, "mid": v(38.6, 3.18) * mm, "end": v(39.14, 3.14) * mm});
            skLineSegment(sketch, "E117.9.0.0", {"start": v(38.2, 5.5) * mm, "end": v(36.1, 3.72) * mm});
            skArc(sketch, "E117.9.0.1", {"start": v(38.7, 4.92) * mm, "mid": v(38.74, 5.45) * mm, "end": v(38.2, 5.5) * mm});
            skLineSegment(sketch, "E117.9.0.2", {"start": v(36.6, 3.14) * mm, "end": v(38.7, 4.92) * mm});
            skArc(sketch, "E117.9.0.3", {"start": v(36.1, 3.72) * mm, "mid": v(36.06, 3.18) * mm, "end": v(36.6, 3.14) * mm});
            skLineSegment(sketch, "E117.10.0.0", {"start": v(35.66, 5.5) * mm, "end": v(33.56, 3.72) * mm});
            skArc(sketch, "E117.10.0.1", {"start": v(36.15, 4.92) * mm, "mid": v(36.2, 5.45) * mm, "end": v(35.66, 5.5) * mm});
            skLineSegment(sketch, "E117.10.0.2", {"start": v(34.06, 3.14) * mm, "end": v(36.15, 4.92) * mm});
            skArc(sketch, "E117.10.0.3", {"start": v(33.56, 3.72) * mm, "mid": v(33.52, 3.18) * mm, "end": v(34.06, 3.14) * mm});
            skLineSegment(sketch, "E117.11.0.0", {"start": v(33.12, 5.5) * mm, "end": v(31.02, 3.72) * mm});
            skArc(sketch, "E117.11.0.1", {"start": v(33.61, 4.92) * mm, "mid": v(33.66, 5.45) * mm, "end": v(33.12, 5.5) * mm});
            skLineSegment(sketch, "E117.11.0.2", {"start": v(31.52, 3.14) * mm, "end": v(33.61, 4.92) * mm});
            skArc(sketch, "E117.11.0.3", {"start": v(31.02, 3.72) * mm, "mid": v(30.98, 3.18) * mm, "end": v(31.52, 3.14) * mm});
            skLineSegment(sketch, "E117.12.0.0", {"start": v(30.58, 5.5) * mm, "end": v(28.48, 3.72) * mm});
            skArc(sketch, "E117.12.0.1", {"start": v(31.07, 4.92) * mm, "mid": v(31.12, 5.45) * mm, "end": v(30.58, 5.5) * mm});
            skLineSegment(sketch, "E117.12.0.2", {"start": v(28.98, 3.14) * mm, "end": v(31.07, 4.92) * mm});
            skArc(sketch, "E117.12.0.3", {"start": v(28.48, 3.72) * mm, "mid": v(28.44, 3.18) * mm, "end": v(28.98, 3.14) * mm});
            skLineSegment(sketch, "E117.13.0.0", {"start": v(28.04, 5.5) * mm, "end": v(25.94, 3.72) * mm});
            skArc(sketch, "E117.13.0.1", {"start": v(28.53, 4.92) * mm, "mid": v(28.58, 5.45) * mm, "end": v(28.04, 5.5) * mm});
            skLineSegment(sketch, "E117.13.0.2", {"start": v(26.44, 3.14) * mm, "end": v(28.53, 4.92) * mm});
            skArc(sketch, "E117.13.0.3", {"start": v(25.94, 3.72) * mm, "mid": v(25.9, 3.18) * mm, "end": v(26.44, 3.14) * mm});
            skLineSegment(sketch, "E117.14.0.0", {"start": v(25.5, 5.5) * mm, "end": v(23.4, 3.72) * mm});
            skArc(sketch, "E117.14.0.1", {"start": v(26, 4.92) * mm, "mid": v(26.04, 5.45) * mm, "end": v(25.5, 5.5) * mm});
            skLineSegment(sketch, "E117.14.0.2", {"start": v(23.9, 3.14) * mm, "end": v(26, 4.92) * mm});
            skArc(sketch, "E117.14.0.3", {"start": v(23.4, 3.72) * mm, "mid": v(23.36, 3.18) * mm, "end": v(23.9, 3.14) * mm});
            skLineSegment(sketch, "E117.15.0.0", {"start": v(22.96, 5.5) * mm, "end": v(20.86, 3.72) * mm});
            skArc(sketch, "E117.15.0.1", {"start": v(23.45, 4.92) * mm, "mid": v(23.5, 5.45) * mm, "end": v(22.96, 5.5) * mm});
            skLineSegment(sketch, "E117.15.0.2", {"start": v(21.36, 3.14) * mm, "end": v(23.45, 4.92) * mm});
            skArc(sketch, "E117.15.0.3", {"start": v(20.86, 3.72) * mm, "mid": v(20.82, 3.18) * mm, "end": v(21.36, 3.14) * mm});
            skLineSegment(sketch, "E117.16.0.0", {"start": v(20.42, 5.5) * mm, "end": v(18.32, 3.72) * mm});
            skArc(sketch, "E117.16.0.1", {"start": v(20.91, 4.92) * mm, "mid": v(20.96, 5.45) * mm, "end": v(20.42, 5.5) * mm});
            skLineSegment(sketch, "E117.16.0.2", {"start": v(18.82, 3.14) * mm, "end": v(20.91, 4.92) * mm});
            skArc(sketch, "E117.16.0.3", {"start": v(18.32, 3.72) * mm, "mid": v(18.28, 3.18) * mm, "end": v(18.82, 3.14) * mm});
            skLineSegment(sketch, "E117.17.0.0", {"start": v(17.88, 5.5) * mm, "end": v(15.78, 3.72) * mm});
            skArc(sketch, "E117.17.0.1", {"start": v(18.37, 4.92) * mm, "mid": v(18.42, 5.45) * mm, "end": v(17.88, 5.5) * mm});
            skLineSegment(sketch, "E117.17.0.2", {"start": v(16.28, 3.14) * mm, "end": v(18.37, 4.92) * mm});
            skArc(sketch, "E117.17.0.3", {"start": v(15.78, 3.72) * mm, "mid": v(15.74, 3.18) * mm, "end": v(16.28, 3.14) * mm});
            skLineSegment(sketch, "E117.18.0.0", {"start": v(15.34, 5.5) * mm, "end": v(13.24, 3.72) * mm});
            skArc(sketch, "E117.18.0.1", {"start": v(15.83, 4.92) * mm, "mid": v(15.88, 5.45) * mm, "end": v(15.34, 5.5) * mm});
            skLineSegment(sketch, "E117.18.0.2", {"start": v(13.74, 3.14) * mm, "end": v(15.83, 4.92) * mm});
            skArc(sketch, "E117.18.0.3", {"start": v(13.24, 3.72) * mm, "mid": v(13.2, 3.18) * mm, "end": v(13.74, 3.14) * mm});
            skLineSegment(sketch, "E117.19.0.0", {"start": v(12.8, 5.5) * mm, "end": v(10.7, 3.72) * mm});
            skArc(sketch, "E117.19.0.1", {"start": v(13.3, 4.92) * mm, "mid": v(13.34, 5.45) * mm, "end": v(12.8, 5.5) * mm});
            skLineSegment(sketch, "E117.19.0.2", {"start": v(11.2, 3.14) * mm, "end": v(13.3, 4.92) * mm});
            skArc(sketch, "E117.19.0.3", {"start": v(10.7, 3.72) * mm, "mid": v(10.66, 3.18) * mm, "end": v(11.2, 3.14) * mm});
            skLineSegment(sketch, "E117.20.0.0", {"start": v(10.26, 5.5) * mm, "end": v(8.16, 3.72) * mm});
            skArc(sketch, "E117.20.0.1", {"start": v(10.75, 4.92) * mm, "mid": v(10.8, 5.45) * mm, "end": v(10.26, 5.5) * mm});
            skLineSegment(sketch, "E117.20.0.2", {"start": v(8.66, 3.14) * mm, "end": v(10.75, 4.92) * mm});
            skArc(sketch, "E117.20.0.3", {"start": v(8.16, 3.72) * mm, "mid": v(8.12, 3.18) * mm, "end": v(8.66, 3.14) * mm});
            skLineSegment(sketch, "E117.21.0.0", {"start": v(7.72, 5.5) * mm, "end": v(5.62, 3.72) * mm});
            skArc(sketch, "E117.21.0.1", {"start": v(8.21, 4.92) * mm, "mid": v(8.26, 5.45) * mm, "end": v(7.72, 5.5) * mm});
            skLineSegment(sketch, "E117.21.0.2", {"start": v(6.12, 3.14) * mm, "end": v(8.21, 4.92) * mm});
            skArc(sketch, "E117.21.0.3", {"start": v(5.62, 3.72) * mm, "mid": v(5.58, 3.18) * mm, "end": v(6.12, 3.14) * mm});
            skLineSegment(sketch, "E117.22.0.0", {"start": v(5.18, 5.5) * mm, "end": v(3.08, 3.72) * mm});
            skArc(sketch, "E117.22.0.1", {"start": v(5.67, 4.92) * mm, "mid": v(5.72, 5.45) * mm, "end": v(5.18, 5.5) * mm});
            skLineSegment(sketch, "E117.22.0.2", {"start": v(3.58, 3.14) * mm, "end": v(5.67, 4.92) * mm});
            skArc(sketch, "E117.22.0.3", {"start": v(3.08, 3.72) * mm, "mid": v(3.04, 3.18) * mm, "end": v(3.58, 3.14) * mm});
            skLineSegment(sketch, "E117.23.0.0", {"start": v(2.64, 5.5) * mm, "end": v(0.54, 3.72) * mm});
            skArc(sketch, "E117.23.0.1", {"start": v(3.13, 4.92) * mm, "mid": v(3.18, 5.45) * mm, "end": v(2.64, 5.5) * mm});
            skLineSegment(sketch, "E117.23.0.2", {"start": v(1.04, 3.14) * mm, "end": v(3.13, 4.92) * mm});
            skArc(sketch, "E117.23.0.3", {"start": v(0.54, 3.72) * mm, "mid": v(0.5, 3.18) * mm, "end": v(1.04, 3.14) * mm});
            skLineSegment(sketch, "E117.24.0.0", {"start": v(0.1, 5.5) * mm, "end": v(-2, 3.72) * mm});
            skArc(sketch, "E117.24.0.1", {"start": v(0.6, 4.92) * mm, "mid": v(0.64, 5.45) * mm, "end": v(0.1, 5.5) * mm});
            skLineSegment(sketch, "E117.24.0.2", {"start": v(-1.5, 3.14) * mm, "end": v(0.6, 4.92) * mm});
            skArc(sketch, "E117.24.0.3", {"start": v(-2, 3.72) * mm, "mid": v(-2.04, 3.18) * mm, "end": v(-1.5, 3.14) * mm});
            skLineSegment(sketch, "E117.25.0.0", {"start": v(-2.44, 5.5) * mm, "end": v(-4.54, 3.72) * mm});
            skArc(sketch, "E117.25.0.1", {"start": v(-1.95, 4.92) * mm, "mid": v(-1.9, 5.45) * mm, "end": v(-2.44, 5.5) * mm});
            skLineSegment(sketch, "E117.25.0.2", {"start": v(-4.04, 3.14) * mm, "end": v(-1.95, 4.92) * mm});
            skArc(sketch, "E117.25.0.3", {"start": v(-4.54, 3.72) * mm, "mid": v(-4.58, 3.18) * mm, "end": v(-4.04, 3.14) * mm});
            skLineSegment(sketch, "E117.26.0.0", {"start": v(-4.98, 5.5) * mm, "end": v(-7.08, 3.72) * mm});
            skArc(sketch, "E117.26.0.1", {"start": v(-4.49, 4.92) * mm, "mid": v(-4.44, 5.45) * mm, "end": v(-4.98, 5.5) * mm});
            skLineSegment(sketch, "E117.26.0.2", {"start": v(-6.58, 3.14) * mm, "end": v(-4.49, 4.92) * mm});
            skArc(sketch, "E117.26.0.3", {"start": v(-7.08, 3.72) * mm, "mid": v(-7.12, 3.18) * mm, "end": v(-6.58, 3.14) * mm});
            skLineSegment(sketch, "E117.27.0.0", {"start": v(-7.52, 5.5) * mm, "end": v(-9.62, 3.72) * mm});
            skArc(sketch, "E117.27.0.1", {"start": v(-7.03, 4.92) * mm, "mid": v(-6.98, 5.45) * mm, "end": v(-7.52, 5.5) * mm});
            skLineSegment(sketch, "E117.27.0.2", {"start": v(-9.12, 3.14) * mm, "end": v(-7.03, 4.92) * mm});
            skArc(sketch, "E117.27.0.3", {"start": v(-9.62, 3.72) * mm, "mid": v(-9.66, 3.18) * mm, "end": v(-9.12, 3.14) * mm});
            skLineSegment(sketch, "E117.28.0.0", {"start": v(-10.06, 5.5) * mm, "end": v(-12.16, 3.72) * mm});
            skArc(sketch, "E117.28.0.1", {"start": v(-9.57, 4.92) * mm, "mid": v(-9.52, 5.45) * mm, "end": v(-10.06, 5.5) * mm});
            skLineSegment(sketch, "E117.28.0.2", {"start": v(-11.66, 3.14) * mm, "end": v(-9.57, 4.92) * mm});
            skArc(sketch, "E117.28.0.3", {"start": v(-12.16, 3.72) * mm, "mid": v(-12.2, 3.18) * mm, "end": v(-11.66, 3.14) * mm});
            skLineSegment(sketch, "E117.29.0.0", {"start": v(-12.6, 5.5) * mm, "end": v(-14.7, 3.72) * mm});
            skArc(sketch, "E117.29.0.1", {"start": v(-12.1, 4.92) * mm, "mid": v(-12.06, 5.45) * mm, "end": v(-12.6, 5.5) * mm});
            skLineSegment(sketch, "E117.29.0.2", {"start": v(-14.2, 3.14) * mm, "end": v(-12.1, 4.92) * mm});
            skArc(sketch, "E117.29.0.3", {"start": v(-14.7, 3.72) * mm, "mid": v(-14.74, 3.18) * mm, "end": v(-14.2, 3.14) * mm});
            skLineSegment(sketch, "E117.30.0.0", {"start": v(-15.14, 5.5) * mm, "end": v(-17.24, 3.72) * mm});
            skArc(sketch, "E117.30.0.1", {"start": v(-14.65, 4.92) * mm, "mid": v(-14.6, 5.45) * mm, "end": v(-15.14, 5.5) * mm});
            skLineSegment(sketch, "E117.30.0.2", {"start": v(-16.74, 3.14) * mm, "end": v(-14.65, 4.92) * mm});
            skArc(sketch, "E117.30.0.3", {"start": v(-17.24, 3.72) * mm, "mid": v(-17.28, 3.18) * mm, "end": v(-16.74, 3.14) * mm});
            skLineSegment(sketch, "E117.direction1", {"start": v(58.96, 3.72) * mm, "end": v(56.42, 3.72) * mm, "construction": true});
            skLineSegment(sketch, "E118", {"start": v(-57.08, 6.1) * mm, "end": v(-18.98, 6.1) * mm, "construction": true});
            skLineSegment(sketch, "E119", {"start": v(-57.08, 4.32) * mm, "end": v(-18.98, 4.32) * mm, "construction": true});
            skLineSegment(sketch, "E120.rect.bottom", {"start": v(-54.28, 4.83) * mm, "end": v(-50.47, 4.83) * mm});
            skLineSegment(sketch, "E120.rect.top", {"start": v(-54.28, 3.8) * mm, "end": v(-50.47, 3.8) * mm});
            skLineSegment(sketch, "E120.rect.left", {"start": v(-54.28, 4.83) * mm, "end": v(-54.28, 3.81) * mm});
            skLineSegment(sketch, "E120.rect.right", {"start": v(-50.47, 4.83) * mm, "end": v(-50.47, 3.81) * mm});
            skPoint(sketch, "E120.rect.middle", {"position": v(-52.37, 4.32) * mm});
            skLineSegment(sketch, "E121.rect.bottom", {"start": v(-23.95, 4.83) * mm, "end": v(-46.81, 4.83) * mm});
            skLineSegment(sketch, "E121.rect.top", {"start": v(-23.95, 3.81) * mm, "end": v(-46.81, 3.81) * mm});
            skLineSegment(sketch, "E121.rect.left", {"start": v(-23.95, 4.83) * mm, "end": v(-23.95, 3.81) * mm});
            skLineSegment(sketch, "E121.rect.right", {"start": v(-46.81, 4.83) * mm, "end": v(-46.81, 3.81) * mm});
            skPoint(sketch, "E121.rect.middle", {"position": v(-35.38, 4.32) * mm});
            skSolve(sketch);
        }
        {
            var Q0;
            Q0=makeQuery(id+"F1.opExtrude","SWEPT_FACE",FACE,{"disambiguationData":[OSD([sQuery(id+"F0.wireOp",EDGE,"E0.right")])]});
            var sketch = newSketch(context, id + "F18", { "sketchPlane" : qUnion([Q0])});
            skLineSegment(sketch, "E122", {"start": v(-62.3, 3.54) * mm, "end": v(-61.3, 3.54) * mm, "construction": true});
            skLineSegment(sketch, "E123", {"start": v(-61.3, 2.54) * mm, "end": v(-61.3, 6.1) * mm, "construction": true});
            skLineSegment(sketch, "E124", {"start": v(-61.3, 4.32) * mm, "end": v(-59.2, 4.32) * mm, "construction": true});
            skLineSegment(sketch, "E125", {"start": v(-59.2, 2.54) * mm, "end": v(-59.2, 6.1) * mm, "construction": true});
            skLineSegment(sketch, "E126", {"start": v(-61.3, 4.32) * mm, "end": v(-61.3, 5.2) * mm, "construction": true});
            skLineSegment(sketch, "E127", {"start": v(-59.2, 4.32) * mm, "end": v(-59.2, 3.43) * mm, "construction": true});
            skLineSegment(sketch, "E128", {"start": v(-61.3, 5.2) * mm, "end": v(-59.2, 3.43) * mm, "construction": true});
            skLineSegment(sketch, "E129", {"start": v(-59.2, 3.43) * mm, "end": v(-58.72, 4.01) * mm, "construction": true});
            skLineSegment(sketch, "E130", {"start": v(-61.3, 5.2) * mm, "end": v(-60.81, 5.79) * mm, "construction": true});
            skLineSegment(sketch, "E131", {"start": v(-60.81, 5.79) * mm, "end": v(-58.72, 4.01) * mm, "construction": true});
            skLineSegment(sketch, "E132", {"start": v(-61.06, 5.5) * mm, "end": v(-58.96, 3.72) * mm});
            skLineSegment(sketch, "E133", {"start": v(-61.55, 4.92) * mm, "end": v(-59.46, 3.14) * mm});
            skArc(sketch, "E134", {"start": v(-61.06, 5.5) * mm, "mid": v(-61.6, 5.45) * mm, "end": v(-61.55, 4.92) * mm});
            skArc(sketch, "E135", {"start": v(-59.46, 3.14) * mm, "mid": v(-58.92, 3.18) * mm, "end": v(-58.96, 3.72) * mm});
            skLineSegment(sketch, "E136.1.0.0", {"start": v(-58.52, 5.5) * mm, "end": v(-56.42, 3.72) * mm});
            skArc(sketch, "E136.1.0.1", {"start": v(-58.52, 5.5) * mm, "mid": v(-59.06, 5.45) * mm, "end": v(-59.01, 4.92) * mm});
            skLineSegment(sketch, "E136.1.0.2", {"start": v(-59.01, 4.92) * mm, "end": v(-56.92, 3.14) * mm});
            skArc(sketch, "E136.1.0.3", {"start": v(-56.92, 3.14) * mm, "mid": v(-56.38, 3.18) * mm, "end": v(-56.42, 3.72) * mm});
            skLineSegment(sketch, "E136.2.0.0", {"start": v(-55.98, 5.5) * mm, "end": v(-53.88, 3.72) * mm});
            skArc(sketch, "E136.2.0.1", {"start": v(-55.98, 5.5) * mm, "mid": v(-56.52, 5.45) * mm, "end": v(-56.47, 4.92) * mm});
            skLineSegment(sketch, "E136.2.0.2", {"start": v(-56.47, 4.92) * mm, "end": v(-54.38, 3.14) * mm});
            skArc(sketch, "E136.2.0.3", {"start": v(-54.38, 3.14) * mm, "mid": v(-53.84, 3.18) * mm, "end": v(-53.88, 3.72) * mm});
            skLineSegment(sketch, "E136.3.0.0", {"start": v(-53.44, 5.5) * mm, "end": v(-51.34, 3.72) * mm});
            skArc(sketch, "E136.3.0.1", {"start": v(-53.44, 5.5) * mm, "mid": v(-53.98, 5.45) * mm, "end": v(-53.93, 4.92) * mm});
            skLineSegment(sketch, "E136.3.0.2", {"start": v(-53.93, 4.92) * mm, "end": v(-51.84, 3.14) * mm});
            skArc(sketch, "E136.3.0.3", {"start": v(-51.84, 3.14) * mm, "mid": v(-51.3, 3.18) * mm, "end": v(-51.34, 3.72) * mm});
            skLineSegment(sketch, "E136.4.0.0", {"start": v(-50.9, 5.5) * mm, "end": v(-48.8, 3.72) * mm});
            skArc(sketch, "E136.4.0.1", {"start": v(-50.9, 5.5) * mm, "mid": v(-51.44, 5.45) * mm, "end": v(-51.4, 4.92) * mm});
            skLineSegment(sketch, "E136.4.0.2", {"start": v(-51.4, 4.92) * mm, "end": v(-49.3, 3.14) * mm});
            skArc(sketch, "E136.4.0.3", {"start": v(-49.3, 3.14) * mm, "mid": v(-48.76, 3.18) * mm, "end": v(-48.8, 3.72) * mm});
            skLineSegment(sketch, "E136.5.0.0", {"start": v(-48.36, 5.5) * mm, "end": v(-46.26, 3.72) * mm});
            skArc(sketch, "E136.5.0.1", {"start": v(-48.36, 5.5) * mm, "mid": v(-48.9, 5.45) * mm, "end": v(-48.85, 4.92) * mm});
            skLineSegment(sketch, "E136.5.0.2", {"start": v(-48.85, 4.92) * mm, "end": v(-46.76, 3.14) * mm});
            skArc(sketch, "E136.5.0.3", {"start": v(-46.76, 3.14) * mm, "mid": v(-46.22, 3.18) * mm, "end": v(-46.26, 3.72) * mm});
            skLineSegment(sketch, "E136.6.0.0", {"start": v(-45.82, 5.5) * mm, "end": v(-43.72, 3.72) * mm});
            skArc(sketch, "E136.6.0.1", {"start": v(-45.82, 5.5) * mm, "mid": v(-46.36, 5.45) * mm, "end": v(-46.31, 4.92) * mm});
            skLineSegment(sketch, "E136.6.0.2", {"start": v(-46.31, 4.92) * mm, "end": v(-44.22, 3.14) * mm});
            skArc(sketch, "E136.6.0.3", {"start": v(-44.22, 3.14) * mm, "mid": v(-43.68, 3.18) * mm, "end": v(-43.72, 3.72) * mm});
            skLineSegment(sketch, "E136.7.0.0", {"start": v(-43.28, 5.5) * mm, "end": v(-41.18, 3.72) * mm});
            skArc(sketch, "E136.7.0.1", {"start": v(-43.28, 5.5) * mm, "mid": v(-43.82, 5.45) * mm, "end": v(-43.77, 4.92) * mm});
            skLineSegment(sketch, "E136.7.0.2", {"start": v(-43.77, 4.92) * mm, "end": v(-41.68, 3.14) * mm});
            skArc(sketch, "E136.7.0.3", {"start": v(-41.68, 3.14) * mm, "mid": v(-41.14, 3.18) * mm, "end": v(-41.18, 3.72) * mm});
            skLineSegment(sketch, "E136.8.0.0", {"start": v(-40.74, 5.5) * mm, "end": v(-38.64, 3.72) * mm});
            skArc(sketch, "E136.8.0.1", {"start": v(-40.74, 5.5) * mm, "mid": v(-41.28, 5.45) * mm, "end": v(-41.23, 4.92) * mm});
            skLineSegment(sketch, "E136.8.0.2", {"start": v(-41.23, 4.92) * mm, "end": v(-39.14, 3.14) * mm});
            skArc(sketch, "E136.8.0.3", {"start": v(-39.14, 3.14) * mm, "mid": v(-38.6, 3.18) * mm, "end": v(-38.64, 3.72) * mm});
            skLineSegment(sketch, "E136.9.0.0", {"start": v(-38.2, 5.5) * mm, "end": v(-36.1, 3.72) * mm});
            skArc(sketch, "E136.9.0.1", {"start": v(-38.2, 5.5) * mm, "mid": v(-38.74, 5.45) * mm, "end": v(-38.7, 4.92) * mm});
            skLineSegment(sketch, "E136.9.0.2", {"start": v(-38.7, 4.92) * mm, "end": v(-36.6, 3.14) * mm});
            skArc(sketch, "E136.9.0.3", {"start": v(-36.6, 3.14) * mm, "mid": v(-36.06, 3.18) * mm, "end": v(-36.1, 3.72) * mm});
            skLineSegment(sketch, "E136.10.0.0", {"start": v(-35.66, 5.5) * mm, "end": v(-33.56, 3.72) * mm});
            skArc(sketch, "E136.10.0.1", {"start": v(-35.66, 5.5) * mm, "mid": v(-36.2, 5.45) * mm, "end": v(-36.15, 4.92) * mm});
            skLineSegment(sketch, "E136.10.0.2", {"start": v(-36.15, 4.92) * mm, "end": v(-34.06, 3.14) * mm});
            skArc(sketch, "E136.10.0.3", {"start": v(-34.06, 3.14) * mm, "mid": v(-33.52, 3.18) * mm, "end": v(-33.56, 3.72) * mm});
            skLineSegment(sketch, "E136.11.0.0", {"start": v(-33.12, 5.5) * mm, "end": v(-31.02, 3.72) * mm});
            skArc(sketch, "E136.11.0.1", {"start": v(-33.12, 5.5) * mm, "mid": v(-33.66, 5.45) * mm, "end": v(-33.61, 4.92) * mm});
            skLineSegment(sketch, "E136.11.0.2", {"start": v(-33.61, 4.92) * mm, "end": v(-31.52, 3.14) * mm});
            skArc(sketch, "E136.11.0.3", {"start": v(-31.52, 3.14) * mm, "mid": v(-30.98, 3.18) * mm, "end": v(-31.02, 3.72) * mm});
            skLineSegment(sketch, "E136.12.0.0", {"start": v(-30.58, 5.5) * mm, "end": v(-28.48, 3.72) * mm});
            skArc(sketch, "E136.12.0.1", {"start": v(-30.58, 5.5) * mm, "mid": v(-31.12, 5.45) * mm, "end": v(-31.07, 4.92) * mm});
            skLineSegment(sketch, "E136.12.0.2", {"start": v(-31.07, 4.92) * mm, "end": v(-28.98, 3.14) * mm});
            skArc(sketch, "E136.12.0.3", {"start": v(-28.98, 3.14) * mm, "mid": v(-28.44, 3.18) * mm, "end": v(-28.48, 3.72) * mm});
            skLineSegment(sketch, "E136.13.0.0", {"start": v(-28.04, 5.5) * mm, "end": v(-25.94, 3.72) * mm});
            skArc(sketch, "E136.13.0.1", {"start": v(-28.04, 5.5) * mm, "mid": v(-28.58, 5.45) * mm, "end": v(-28.53, 4.92) * mm});
            skLineSegment(sketch, "E136.13.0.2", {"start": v(-28.53, 4.92) * mm, "end": v(-26.44, 3.14) * mm});
            skArc(sketch, "E136.13.0.3", {"start": v(-26.44, 3.14) * mm, "mid": v(-25.9, 3.18) * mm, "end": v(-25.94, 3.72) * mm});
            skLineSegment(sketch, "E136.14.0.0", {"start": v(-25.5, 5.5) * mm, "end": v(-23.4, 3.72) * mm});
            skArc(sketch, "E136.14.0.1", {"start": v(-25.5, 5.5) * mm, "mid": v(-26.04, 5.45) * mm, "end": v(-26, 4.92) * mm});
            skLineSegment(sketch, "E136.14.0.2", {"start": v(-26, 4.92) * mm, "end": v(-23.9, 3.14) * mm});
            skArc(sketch, "E136.14.0.3", {"start": v(-23.9, 3.14) * mm, "mid": v(-23.36, 3.18) * mm, "end": v(-23.4, 3.72) * mm});
            skLineSegment(sketch, "E136.15.0.0", {"start": v(-22.96, 5.5) * mm, "end": v(-20.86, 3.72) * mm});
            skArc(sketch, "E136.15.0.1", {"start": v(-22.96, 5.5) * mm, "mid": v(-23.5, 5.45) * mm, "end": v(-23.45, 4.92) * mm});
            skLineSegment(sketch, "E136.15.0.2", {"start": v(-23.45, 4.92) * mm, "end": v(-21.36, 3.14) * mm});
            skArc(sketch, "E136.15.0.3", {"start": v(-21.36, 3.14) * mm, "mid": v(-20.82, 3.18) * mm, "end": v(-20.86, 3.72) * mm});
            skLineSegment(sketch, "E136.16.0.0", {"start": v(-20.42, 5.5) * mm, "end": v(-18.32, 3.72) * mm});
            skArc(sketch, "E136.16.0.1", {"start": v(-20.42, 5.5) * mm, "mid": v(-20.96, 5.45) * mm, "end": v(-20.91, 4.92) * mm});
            skLineSegment(sketch, "E136.16.0.2", {"start": v(-20.91, 4.92) * mm, "end": v(-18.82, 3.14) * mm});
            skArc(sketch, "E136.16.0.3", {"start": v(-18.82, 3.14) * mm, "mid": v(-18.28, 3.18) * mm, "end": v(-18.32, 3.72) * mm});
            skLineSegment(sketch, "E136.17.0.0", {"start": v(-17.88, 5.5) * mm, "end": v(-15.78, 3.72) * mm});
            skArc(sketch, "E136.17.0.1", {"start": v(-17.88, 5.5) * mm, "mid": v(-18.42, 5.45) * mm, "end": v(-18.37, 4.92) * mm});
            skLineSegment(sketch, "E136.17.0.2", {"start": v(-18.37, 4.92) * mm, "end": v(-16.28, 3.14) * mm});
            skArc(sketch, "E136.17.0.3", {"start": v(-16.28, 3.14) * mm, "mid": v(-15.74, 3.18) * mm, "end": v(-15.78, 3.72) * mm});
            skLineSegment(sketch, "E136.18.0.0", {"start": v(-15.34, 5.5) * mm, "end": v(-13.24, 3.72) * mm});
            skArc(sketch, "E136.18.0.1", {"start": v(-15.34, 5.5) * mm, "mid": v(-15.88, 5.45) * mm, "end": v(-15.83, 4.92) * mm});
            skLineSegment(sketch, "E136.18.0.2", {"start": v(-15.83, 4.92) * mm, "end": v(-13.74, 3.14) * mm});
            skArc(sketch, "E136.18.0.3", {"start": v(-13.74, 3.14) * mm, "mid": v(-13.2, 3.18) * mm, "end": v(-13.24, 3.72) * mm});
            skLineSegment(sketch, "E136.19.0.0", {"start": v(-12.8, 5.5) * mm, "end": v(-10.7, 3.72) * mm});
            skArc(sketch, "E136.19.0.1", {"start": v(-12.8, 5.5) * mm, "mid": v(-13.34, 5.45) * mm, "end": v(-13.3, 4.92) * mm});
            skLineSegment(sketch, "E136.19.0.2", {"start": v(-13.3, 4.92) * mm, "end": v(-11.2, 3.14) * mm});
            skArc(sketch, "E136.19.0.3", {"start": v(-11.2, 3.14) * mm, "mid": v(-10.66, 3.18) * mm, "end": v(-10.7, 3.72) * mm});
            skLineSegment(sketch, "E136.20.0.0", {"start": v(-10.26, 5.5) * mm, "end": v(-8.16, 3.72) * mm});
            skArc(sketch, "E136.20.0.1", {"start": v(-10.26, 5.5) * mm, "mid": v(-10.8, 5.45) * mm, "end": v(-10.75, 4.92) * mm});
            skLineSegment(sketch, "E136.20.0.2", {"start": v(-10.75, 4.92) * mm, "end": v(-8.66, 3.14) * mm});
            skArc(sketch, "E136.20.0.3", {"start": v(-8.66, 3.14) * mm, "mid": v(-8.12, 3.18) * mm, "end": v(-8.16, 3.72) * mm});
            skLineSegment(sketch, "E136.21.0.0", {"start": v(-7.72, 5.5) * mm, "end": v(-5.62, 3.72) * mm});
            skArc(sketch, "E136.21.0.1", {"start": v(-7.72, 5.5) * mm, "mid": v(-8.26, 5.45) * mm, "end": v(-8.21, 4.92) * mm});
            skLineSegment(sketch, "E136.21.0.2", {"start": v(-8.21, 4.92) * mm, "end": v(-6.12, 3.14) * mm});
            skArc(sketch, "E136.21.0.3", {"start": v(-6.12, 3.14) * mm, "mid": v(-5.58, 3.18) * mm, "end": v(-5.62, 3.72) * mm});
            skLineSegment(sketch, "E136.22.0.0", {"start": v(-5.18, 5.5) * mm, "end": v(-3.08, 3.72) * mm});
            skArc(sketch, "E136.22.0.1", {"start": v(-5.18, 5.5) * mm, "mid": v(-5.72, 5.45) * mm, "end": v(-5.67, 4.92) * mm});
            skLineSegment(sketch, "E136.22.0.2", {"start": v(-5.67, 4.92) * mm, "end": v(-3.58, 3.14) * mm});
            skArc(sketch, "E136.22.0.3", {"start": v(-3.58, 3.14) * mm, "mid": v(-3.04, 3.18) * mm, "end": v(-3.08, 3.72) * mm});
            skLineSegment(sketch, "E136.23.0.0", {"start": v(-2.64, 5.5) * mm, "end": v(-0.54, 3.72) * mm});
            skArc(sketch, "E136.23.0.1", {"start": v(-2.64, 5.5) * mm, "mid": v(-3.18, 5.45) * mm, "end": v(-3.13, 4.92) * mm});
            skLineSegment(sketch, "E136.23.0.2", {"start": v(-3.13, 4.92) * mm, "end": v(-1.04, 3.14) * mm});
            skArc(sketch, "E136.23.0.3", {"start": v(-1.04, 3.14) * mm, "mid": v(-0.5, 3.18) * mm, "end": v(-0.54, 3.72) * mm});
            skLineSegment(sketch, "E136.24.0.0", {"start": v(-0.1, 5.5) * mm, "end": v(2, 3.72) * mm});
            skArc(sketch, "E136.24.0.1", {"start": v(-0.1, 5.5) * mm, "mid": v(-0.64, 5.45) * mm, "end": v(-0.6, 4.92) * mm});
            skLineSegment(sketch, "E136.24.0.2", {"start": v(-0.6, 4.92) * mm, "end": v(1.5, 3.14) * mm});
            skArc(sketch, "E136.24.0.3", {"start": v(1.5, 3.14) * mm, "mid": v(2.04, 3.18) * mm, "end": v(2, 3.72) * mm});
            skLineSegment(sketch, "E136.25.0.0", {"start": v(2.44, 5.5) * mm, "end": v(4.54, 3.72) * mm});
            skArc(sketch, "E136.25.0.1", {"start": v(2.44, 5.5) * mm, "mid": v(1.9, 5.45) * mm, "end": v(1.95, 4.92) * mm});
            skLineSegment(sketch, "E136.25.0.2", {"start": v(1.95, 4.92) * mm, "end": v(4.04, 3.14) * mm});
            skArc(sketch, "E136.25.0.3", {"start": v(4.04, 3.14) * mm, "mid": v(4.58, 3.18) * mm, "end": v(4.54, 3.72) * mm});
            skLineSegment(sketch, "E136.26.0.0", {"start": v(4.98, 5.5) * mm, "end": v(7.08, 3.72) * mm});
            skArc(sketch, "E136.26.0.1", {"start": v(4.98, 5.5) * mm, "mid": v(4.44, 5.45) * mm, "end": v(4.49, 4.92) * mm});
            skLineSegment(sketch, "E136.26.0.2", {"start": v(4.49, 4.92) * mm, "end": v(6.58, 3.14) * mm});
            skArc(sketch, "E136.26.0.3", {"start": v(6.58, 3.14) * mm, "mid": v(7.12, 3.18) * mm, "end": v(7.08, 3.72) * mm});
            skLineSegment(sketch, "E136.27.0.0", {"start": v(7.52, 5.5) * mm, "end": v(9.62, 3.72) * mm});
            skArc(sketch, "E136.27.0.1", {"start": v(7.52, 5.5) * mm, "mid": v(6.98, 5.45) * mm, "end": v(7.03, 4.92) * mm});
            skLineSegment(sketch, "E136.27.0.2", {"start": v(7.03, 4.92) * mm, "end": v(9.12, 3.14) * mm});
            skArc(sketch, "E136.27.0.3", {"start": v(9.12, 3.14) * mm, "mid": v(9.66, 3.18) * mm, "end": v(9.62, 3.72) * mm});
            skLineSegment(sketch, "E136.28.0.0", {"start": v(10.06, 5.5) * mm, "end": v(12.16, 3.72) * mm});
            skArc(sketch, "E136.28.0.1", {"start": v(10.06, 5.5) * mm, "mid": v(9.52, 5.45) * mm, "end": v(9.57, 4.92) * mm});
            skLineSegment(sketch, "E136.28.0.2", {"start": v(9.57, 4.92) * mm, "end": v(11.66, 3.14) * mm});
            skArc(sketch, "E136.28.0.3", {"start": v(11.66, 3.14) * mm, "mid": v(12.2, 3.18) * mm, "end": v(12.16, 3.72) * mm});
            skLineSegment(sketch, "E136.29.0.0", {"start": v(12.6, 5.5) * mm, "end": v(14.7, 3.72) * mm});
            skArc(sketch, "E136.29.0.1", {"start": v(12.6, 5.5) * mm, "mid": v(12.06, 5.45) * mm, "end": v(12.1, 4.92) * mm});
            skLineSegment(sketch, "E136.29.0.2", {"start": v(12.1, 4.92) * mm, "end": v(14.2, 3.14) * mm});
            skArc(sketch, "E136.29.0.3", {"start": v(14.2, 3.14) * mm, "mid": v(14.74, 3.18) * mm, "end": v(14.7, 3.72) * mm});
            skLineSegment(sketch, "E136.30.0.0", {"start": v(15.14, 5.5) * mm, "end": v(17.24, 3.72) * mm});
            skArc(sketch, "E136.30.0.1", {"start": v(15.14, 5.5) * mm, "mid": v(14.6, 5.45) * mm, "end": v(14.65, 4.92) * mm});
            skLineSegment(sketch, "E136.30.0.2", {"start": v(14.65, 4.92) * mm, "end": v(16.74, 3.14) * mm});
            skArc(sketch, "E136.30.0.3", {"start": v(16.74, 3.14) * mm, "mid": v(17.28, 3.18) * mm, "end": v(17.24, 3.72) * mm});
            skLineSegment(sketch, "E136.31.0.0", {"start": v(17.68, 5.5) * mm, "end": v(19.78, 3.72) * mm});
            skArc(sketch, "E136.31.0.1", {"start": v(17.68, 5.5) * mm, "mid": v(17.14, 5.45) * mm, "end": v(17.19, 4.92) * mm});
            skLineSegment(sketch, "E136.31.0.2", {"start": v(17.19, 4.92) * mm, "end": v(19.28, 3.14) * mm});
            skArc(sketch, "E136.31.0.3", {"start": v(19.28, 3.14) * mm, "mid": v(19.82, 3.18) * mm, "end": v(19.78, 3.72) * mm});
            skLineSegment(sketch, "E136.37.0.0", {"start": v(32.92, 5.5) * mm, "end": v(35.02, 3.72) * mm});
            skArc(sketch, "E136.37.0.1", {"start": v(32.92, 5.5) * mm, "mid": v(32.38, 5.45) * mm, "end": v(32.43, 4.92) * mm});
            skLineSegment(sketch, "E136.37.0.2", {"start": v(32.43, 4.92) * mm, "end": v(34.52, 3.14) * mm});
            skArc(sketch, "E136.37.0.3", {"start": v(34.52, 3.14) * mm, "mid": v(35.06, 3.18) * mm, "end": v(35.02, 3.72) * mm});
            skLineSegment(sketch, "E136.38.0.0", {"start": v(35.46, 5.5) * mm, "end": v(37.56, 3.72) * mm});
            skArc(sketch, "E136.38.0.1", {"start": v(35.46, 5.5) * mm, "mid": v(34.92, 5.45) * mm, "end": v(34.97, 4.92) * mm});
            skLineSegment(sketch, "E136.38.0.2", {"start": v(34.97, 4.92) * mm, "end": v(37.06, 3.14) * mm});
            skArc(sketch, "E136.38.0.3", {"start": v(37.06, 3.14) * mm, "mid": v(37.6, 3.18) * mm, "end": v(37.56, 3.72) * mm});
            skLineSegment(sketch, "E136.39.0.0", {"start": v(38, 5.5) * mm, "end": v(40.1, 3.72) * mm});
            skArc(sketch, "E136.39.0.1", {"start": v(38, 5.5) * mm, "mid": v(37.46, 5.45) * mm, "end": v(37.5, 4.92) * mm});
            skLineSegment(sketch, "E136.39.0.2", {"start": v(37.5, 4.92) * mm, "end": v(39.6, 3.14) * mm});
            skArc(sketch, "E136.39.0.3", {"start": v(39.6, 3.14) * mm, "mid": v(40.14, 3.18) * mm, "end": v(40.1, 3.72) * mm});
            skLineSegment(sketch, "E136.40.0.0", {"start": v(40.54, 5.5) * mm, "end": v(42.64, 3.72) * mm});
            skArc(sketch, "E136.40.0.1", {"start": v(40.54, 5.5) * mm, "mid": v(40, 5.45) * mm, "end": v(40.05, 4.92) * mm});
            skLineSegment(sketch, "E136.40.0.2", {"start": v(40.05, 4.92) * mm, "end": v(42.14, 3.14) * mm});
            skArc(sketch, "E136.40.0.3", {"start": v(42.14, 3.14) * mm, "mid": v(42.68, 3.18) * mm, "end": v(42.64, 3.72) * mm});
            skLineSegment(sketch, "E136.41.0.0", {"start": v(43.08, 5.5) * mm, "end": v(45.18, 3.72) * mm});
            skArc(sketch, "E136.41.0.1", {"start": v(43.08, 5.5) * mm, "mid": v(42.54, 5.45) * mm, "end": v(42.59, 4.92) * mm});
            skLineSegment(sketch, "E136.41.0.2", {"start": v(42.59, 4.92) * mm, "end": v(44.68, 3.14) * mm});
            skArc(sketch, "E136.41.0.3", {"start": v(44.68, 3.14) * mm, "mid": v(45.22, 3.18) * mm, "end": v(45.18, 3.72) * mm});
            skLineSegment(sketch, "E136.42.0.0", {"start": v(45.62, 5.5) * mm, "end": v(47.72, 3.72) * mm});
            skArc(sketch, "E136.42.0.1", {"start": v(45.62, 5.5) * mm, "mid": v(45.08, 5.45) * mm, "end": v(45.13, 4.92) * mm});
            skLineSegment(sketch, "E136.42.0.2", {"start": v(45.13, 4.92) * mm, "end": v(47.22, 3.14) * mm});
            skArc(sketch, "E136.42.0.3", {"start": v(47.22, 3.14) * mm, "mid": v(47.76, 3.18) * mm, "end": v(47.72, 3.72) * mm});
            skLineSegment(sketch, "E136.43.0.0", {"start": v(48.16, 5.5) * mm, "end": v(50.26, 3.72) * mm});
            skArc(sketch, "E136.43.0.1", {"start": v(48.16, 5.5) * mm, "mid": v(47.62, 5.45) * mm, "end": v(47.67, 4.92) * mm});
            skLineSegment(sketch, "E136.43.0.2", {"start": v(47.67, 4.92) * mm, "end": v(49.76, 3.14) * mm});
            skArc(sketch, "E136.43.0.3", {"start": v(49.76, 3.14) * mm, "mid": v(50.3, 3.18) * mm, "end": v(50.26, 3.72) * mm});
            skLineSegment(sketch, "E136.44.0.0", {"start": v(50.7, 5.5) * mm, "end": v(52.8, 3.72) * mm});
            skArc(sketch, "E136.44.0.1", {"start": v(50.7, 5.5) * mm, "mid": v(50.16, 5.45) * mm, "end": v(50.2, 4.92) * mm});
            skLineSegment(sketch, "E136.44.0.2", {"start": v(50.2, 4.92) * mm, "end": v(52.3, 3.14) * mm});
            skArc(sketch, "E136.44.0.3", {"start": v(52.3, 3.14) * mm, "mid": v(52.84, 3.18) * mm, "end": v(52.8, 3.72) * mm});
            skLineSegment(sketch, "E136.45.0.0", {"start": v(53.24, 5.5) * mm, "end": v(55.34, 3.72) * mm});
            skArc(sketch, "E136.45.0.1", {"start": v(53.24, 5.5) * mm, "mid": v(52.7, 5.45) * mm, "end": v(52.75, 4.92) * mm});
            skLineSegment(sketch, "E136.45.0.2", {"start": v(52.75, 4.92) * mm, "end": v(54.84, 3.14) * mm});
            skArc(sketch, "E136.45.0.3", {"start": v(54.84, 3.14) * mm, "mid": v(55.38, 3.18) * mm, "end": v(55.34, 3.72) * mm});
            skLineSegment(sketch, "E136.direction1", {"start": v(-61.06, 5.5) * mm, "end": v(-58.52, 5.5) * mm, "construction": true});
            skLineSegment(sketch, "E137", {"start": v(57.08, 6.1) * mm, "end": v(31.68, 6.1) * mm, "construction": true});
            skLineSegment(sketch, "E138", {"start": v(33.48, 4.03) * mm, "end": v(20.78, 4.03) * mm, "construction": true});
            skPoint(sketch, "E139.orphan", {"position": v(21.82, 3.14) * mm});
            skLineSegment(sketch, "E140.top", {"start": v(20.78, 4.7) * mm, "end": v(31.89, 4.7) * mm});
            skLineSegment(sketch, "E140.left", {"start": v(20.78, 4.03) * mm, "end": v(20.78, 4.7) * mm});
            skLineSegment(sketch, "E140.right", {"start": v(31.89, 4.03) * mm, "end": v(31.89, 4.7) * mm});
            skLineSegment(sketch, "E141.MirrorCS", {"start": v(31.89, 4.03) * mm, "end": v(31.89, 3.35) * mm});
            skLineSegment(sketch, "E142.MirrorCS", {"start": v(20.78, 3.35) * mm, "end": v(31.89, 3.35) * mm});
            skLineSegment(sketch, "E143.MirrorCS", {"start": v(20.78, 4.03) * mm, "end": v(20.78, 3.35) * mm});
            skSolve(sketch);
        }
        {
            var Q0;
            Q0 = qSketchRegion(id + "F18", true);
            extrude(context, id + "F19", {"entities" : qUnion([Q0]), "operationType" : NewBodyOperationType.REMOVE, "oppositeDirection" : true, "depth" : 0.25 * mm});
        }
        {
            var Q0;
            Q0 = qSketchRegion(id + "F17", true);
            extrude(context, id + "F20", {"entities" : qUnion([Q0]), "operationType" : NewBodyOperationType.REMOVE, "oppositeDirection" : true, "depth" : 0.25 * mm});
        }
        {
            var Q0;
            Q0 = qSketchRegion(id + "F12", true);
            extrude(context, id + "F21", {"entities" : qUnion([Q0]), "depth" : 0.03 * mm});
        }
        {
            var Q0;
            Q0=makeQuery(id+"F1.opExtrude","SWEPT_FACE",FACE,{"disambiguationData":[OSD([sQuery(id+"F0.wireOp",EDGE,"E0.bottom")])]});
            var sketch = newSketch(context, id + "F22", { "sketchPlane" : qUnion([Q0])});
            skLineSegment(sketch, "E144", {"start": v(-6.09, 4.32) * mm, "end": v(42.17, 4.32) * mm, "construction": true});
            skCircle(sketch, "E145", {"center": v(-3.44, 4.32) * mm, "radius": 1.12 * mm});
            skCircle(sketch, "E146", {"center": v(40.84, 3.38) * mm, "radius": 0.43 * mm});
            skSolve(sketch);
        }
        {
            var Q0;
            Q0 = qSketchRegion(id + "F22", true);
            extrude(context, id + "F23", {"entities" : qUnion([Q0]), "operationType" : NewBodyOperationType.REMOVE, "oppositeDirection" : true, "depth" : 7.62 * mm});
        }
        {
            var Q0;
            Q0=makeQuery(id+"F1.opExtrude","CAP_FACE",FACE,{"disambiguationData":[OSD([sQuery(id+"F0.wireOp",EDGE,"E0.bottom"),sQuery(id+"F0.wireOp",EDGE,"E0.top"),sQuery(id+"F0.wireOp",EDGE,"E0.left"),sQuery(id+"F0.wireOp",EDGE,"E0.right")])],"isStart":false});
            var sketch = newSketch(context, id + "F24", { "sketchPlane" : qUnion([Q0])});
            skText(sketch, "E147", { "text": "SAMSUNG", "fontName": "NotoSansCJKsc-Bold.otf"});
            const initialGuessF24  = {"E147": [-0.02654, 0.05775, 1, 0, 0.00247]};
            skSetInitialGuess(sketch, initialGuessF24);
            skSolve(sketch);
        }
        {
            var Q0;
            Q0 = qSketchRegion(id + "F24", true);
            extrude(context, id + "F25", {"entities" : qUnion([Q0]), "operationType" : NewBodyOperationType.REMOVE, "oppositeDirection" : true, "depth" : 0.03 * mm});
        }
        {
            var Q0;
            Q0 = qSketchRegion(id + "F24", true);
            extrude(context, id + "F26", {"entities" : qUnion([Q0]), "depth" : 0.03 * mm});
        }
        {
            var Q0;
            Q0 = qSketchRegion(id + "F14", true);
            var Q1;
            Q1=makeQuery(id+"F13.boolean.opBoolean","SPLIT",FACE,{"disambiguationData":[TD([makeQuery(id+"F13.opExtrude","SWEPT_FACE",FACE,{"disambiguationData":[OSD([sQuery(id+"F12.wireOp",EDGE,"E60.MirrorCS")])]})])],"derivedFrom":makeQuery(id+"F1.opExtrude","CAP_FACE",FACE,{"disambiguationData":[OSD([sQuery(id+"F0.wireOp",EDGE,"E0.bottom"),sQuery(id+"F0.wireOp",EDGE,"E0.top"),sQuery(id+"F0.wireOp",EDGE,"E0.left"),sQuery(id+"F0.wireOp",EDGE,"E0.right")])],"isStart":true})});
            extrude(context, id + "F27", {"entities" : qUnion([Q0, Q1]), "depth" : 0.76 * mm});
        }
        {
            var Q0;
            Q0=makeQuery(id+"F20.boolean.opBoolean","COPY",FACE,{"derivedFrom":makeQuery(id+"F20.opExtrude","CAP_FACE",FACE,{"disambiguationData":[OSD([sQuery(id+"F17.wireOp",EDGE,"E121.rect.bottom"),sQuery(id+"F17.wireOp",EDGE,"E121.rect.top"),sQuery(id+"F17.wireOp",EDGE,"E121.rect.left"),sQuery(id+"F17.wireOp",EDGE,"E121.rect.right")])],"isStart":false})});
            extrude(context, id + "F28", {"entities" : qUnion([Q0]), "depth" : 0.64 * mm});
        }
        {
            var Q0;
            Q0=makeQuery(id+"F20.boolean.opBoolean","COPY",FACE,{"derivedFrom":makeQuery(id+"F20.opExtrude","CAP_FACE",FACE,{"disambiguationData":[OSD([sQuery(id+"F17.wireOp",EDGE,"E120.rect.bottom"),sQuery(id+"F17.wireOp",EDGE,"E120.rect.top"),sQuery(id+"F17.wireOp",EDGE,"E120.rect.left"),sQuery(id+"F17.wireOp",EDGE,"E120.rect.right")])],"isStart":false})});
            extrude(context, id + "F29", {"entities" : qUnion([Q0]), "depth" : 0.5 * mm});
        }
        {
            var Q0;
            Q0=makeQuery(id+"F19.boolean.opBoolean","COPY",FACE,{"derivedFrom":makeQuery(id+"F19.opExtrude","CAP_FACE",FACE,{"disambiguationData":[OSD([sQuery(id+"F18.wireOp",EDGE,"E140.top"),sQuery(id+"F18.wireOp",EDGE,"E140.left"),sQuery(id+"F18.wireOp",EDGE,"E140.right"),sQuery(id+"F18.wireOp",EDGE,"E141.MirrorCS"),sQuery(id+"F18.wireOp",EDGE,"E142.MirrorCS"),sQuery(id+"F18.wireOp",EDGE,"E143.MirrorCS")])],"isStart":false})});
            extrude(context, id + "F30", {"entities" : qUnion([Q0]), "depth" : 0.5 * mm});
        }
    });
